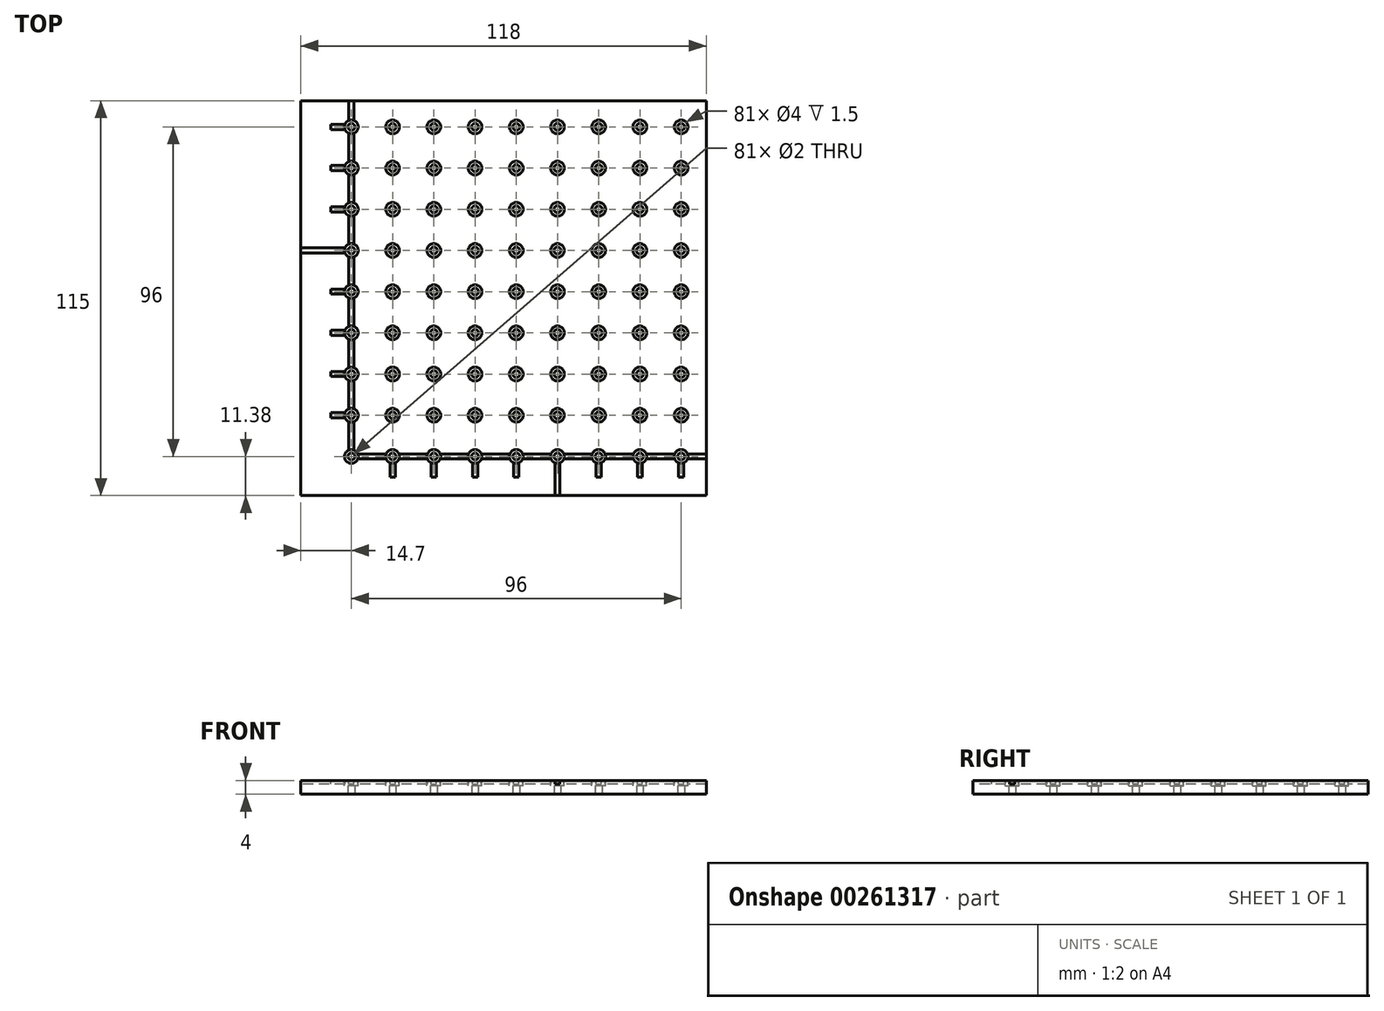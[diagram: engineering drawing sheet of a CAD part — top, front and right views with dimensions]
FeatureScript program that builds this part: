
annotation { "Feature Type Name" : "Feature", "Feature Type Description" : "" }
export const myFeature = defineFeature(function(context is Context, id is Id, definition is map)
    precondition{}
    {
        {
            var Q0;
            Q0=qCreatedBy(makeId("Top.planeOp"),FACE);
            var sketch = newSketch(context, id + "F0", { "sketchPlane" : qUnion([Q0])});
            skLineSegment(sketch, "E0.bottom", {"start": v(-95, -95) * mm, "end": v(95, -95) * mm});
            skLineSegment(sketch, "E0.top", {"start": v(-95, 95) * mm, "end": v(95, 95) * mm});
            skLineSegment(sketch, "E0.left", {"start": v(-95, -95) * mm, "end": v(-95, 95) * mm});
            skLineSegment(sketch, "E0.right", {"start": v(95, -95) * mm, "end": v(95, 95) * mm});
            skPoint(sketch, "E0.middle", {"position": v(0, 0) * mm});
            skCircle(sketch, "E1", {"center": v(-80, 85) * mm, "radius": 1 * mm});
            skCircle(sketch, "E2.0.1.0", {"center": v(-80, 73) * mm, "radius": 1 * mm});
            skCircle(sketch, "E2.0.2.0", {"center": v(-80, 61) * mm, "radius": 1 * mm});
            skCircle(sketch, "E2.0.3.0", {"center": v(-80, 49) * mm, "radius": 1 * mm});
            skCircle(sketch, "E2.0.4.0", {"center": v(-80, 37) * mm, "radius": 1 * mm});
            skCircle(sketch, "E2.0.5.0", {"center": v(-80, 25) * mm, "radius": 1 * mm});
            skCircle(sketch, "E2.0.6.0", {"center": v(-80, 13) * mm, "radius": 1 * mm});
            skCircle(sketch, "E2.0.7.0", {"center": v(-80, 1) * mm, "radius": 1 * mm});
            skCircle(sketch, "E2.0.8.0", {"center": v(-80, -11) * mm, "radius": 1 * mm});
            skCircle(sketch, "E2.0.9.0", {"center": v(-80, -23) * mm, "radius": 1 * mm});
            skCircle(sketch, "E2.0.10.0", {"center": v(-80, -35) * mm, "radius": 1 * mm});
            skCircle(sketch, "E2.0.11.0", {"center": v(-80, -47) * mm, "radius": 1 * mm});
            skCircle(sketch, "E2.0.12.0", {"center": v(-80, -59) * mm, "radius": 1 * mm});
            skCircle(sketch, "E2.0.13.0", {"center": v(-80, -71) * mm, "radius": 1 * mm});
            skCircle(sketch, "E2.0.14.0", {"center": v(-80, -83) * mm, "radius": 1 * mm});
            skLineSegment(sketch, "E2.direction1", {"start": v(-80, 85) * mm, "end": v(-68, 85) * mm, "construction": true});
            skLineSegment(sketch, "E2.direction2", {"start": v(-80, 85) * mm, "end": v(-80, 73) * mm, "construction": true});
            skCircle(sketch, "E3.0.1.0", {"center": v(-68, 85) * mm, "radius": 1 * mm});
            skCircle(sketch, "E3.0.1.1", {"center": v(-68, 73) * mm, "radius": 1 * mm});
            skCircle(sketch, "E3.0.1.2", {"center": v(-68, 61) * mm, "radius": 1 * mm});
            skCircle(sketch, "E3.0.1.3", {"center": v(-68, 49) * mm, "radius": 1 * mm});
            skCircle(sketch, "E3.0.1.4", {"center": v(-68, 37) * mm, "radius": 1 * mm});
            skCircle(sketch, "E3.0.1.5", {"center": v(-68, 25) * mm, "radius": 1 * mm});
            skCircle(sketch, "E3.0.1.6", {"center": v(-68, 13) * mm, "radius": 1 * mm});
            skCircle(sketch, "E3.0.1.7", {"center": v(-68, 1) * mm, "radius": 1 * mm});
            skCircle(sketch, "E3.0.1.8", {"center": v(-68, -11) * mm, "radius": 1 * mm});
            skCircle(sketch, "E3.0.1.9", {"center": v(-68, -23) * mm, "radius": 1 * mm});
            skCircle(sketch, "E3.0.1.10", {"center": v(-68, -35) * mm, "radius": 1 * mm});
            skCircle(sketch, "E3.0.1.11", {"center": v(-68, -47) * mm, "radius": 1 * mm});
            skCircle(sketch, "E3.0.1.12", {"center": v(-68, -59) * mm, "radius": 1 * mm});
            skCircle(sketch, "E3.0.1.13", {"center": v(-68, -71) * mm, "radius": 1 * mm});
            skCircle(sketch, "E3.0.1.14", {"center": v(-68, -83) * mm, "radius": 1 * mm});
            skCircle(sketch, "E3.0.2.0", {"center": v(-56, 85) * mm, "radius": 1 * mm});
            skCircle(sketch, "E3.0.2.1", {"center": v(-56, 73) * mm, "radius": 1 * mm});
            skCircle(sketch, "E3.0.2.2", {"center": v(-56, 61) * mm, "radius": 1 * mm});
            skCircle(sketch, "E3.0.2.3", {"center": v(-56, 49) * mm, "radius": 1 * mm});
            skCircle(sketch, "E3.0.2.4", {"center": v(-56, 37) * mm, "radius": 1 * mm});
            skCircle(sketch, "E3.0.2.5", {"center": v(-56, 25) * mm, "radius": 1 * mm});
            skCircle(sketch, "E3.0.2.6", {"center": v(-56, 13) * mm, "radius": 1 * mm});
            skCircle(sketch, "E3.0.2.7", {"center": v(-56, 1) * mm, "radius": 1 * mm});
            skCircle(sketch, "E3.0.2.8", {"center": v(-56, -11) * mm, "radius": 1 * mm});
            skCircle(sketch, "E3.0.2.9", {"center": v(-56, -23) * mm, "radius": 1 * mm});
            skCircle(sketch, "E3.0.2.10", {"center": v(-56, -35) * mm, "radius": 1 * mm});
            skCircle(sketch, "E3.0.2.11", {"center": v(-56, -47) * mm, "radius": 1 * mm});
            skCircle(sketch, "E3.0.2.12", {"center": v(-56, -59) * mm, "radius": 1 * mm});
            skCircle(sketch, "E3.0.2.13", {"center": v(-56, -71) * mm, "radius": 1 * mm});
            skCircle(sketch, "E3.0.2.14", {"center": v(-56, -83) * mm, "radius": 1 * mm});
            skCircle(sketch, "E3.0.3.0", {"center": v(-44, 85) * mm, "radius": 1 * mm});
            skCircle(sketch, "E3.0.3.1", {"center": v(-44, 73) * mm, "radius": 1 * mm});
            skCircle(sketch, "E3.0.3.2", {"center": v(-44, 61) * mm, "radius": 1 * mm});
            skCircle(sketch, "E3.0.3.3", {"center": v(-44, 49) * mm, "radius": 1 * mm});
            skCircle(sketch, "E3.0.3.4", {"center": v(-44, 37) * mm, "radius": 1 * mm});
            skCircle(sketch, "E3.0.3.5", {"center": v(-44, 25) * mm, "radius": 1 * mm});
            skCircle(sketch, "E3.0.3.6", {"center": v(-44, 13) * mm, "radius": 1 * mm});
            skCircle(sketch, "E3.0.3.7", {"center": v(-44, 1) * mm, "radius": 1 * mm});
            skCircle(sketch, "E3.0.3.8", {"center": v(-44, -11) * mm, "radius": 1 * mm});
            skCircle(sketch, "E3.0.3.9", {"center": v(-44, -23) * mm, "radius": 1 * mm});
            skCircle(sketch, "E3.0.3.10", {"center": v(-44, -35) * mm, "radius": 1 * mm});
            skCircle(sketch, "E3.0.3.11", {"center": v(-44, -47) * mm, "radius": 1 * mm});
            skCircle(sketch, "E3.0.3.12", {"center": v(-44, -59) * mm, "radius": 1 * mm});
            skCircle(sketch, "E3.0.3.13", {"center": v(-44, -71) * mm, "radius": 1 * mm});
            skCircle(sketch, "E3.0.3.14", {"center": v(-44, -83) * mm, "radius": 1 * mm});
            skCircle(sketch, "E3.0.4.0", {"center": v(-32, 85) * mm, "radius": 1 * mm});
            skCircle(sketch, "E3.0.4.1", {"center": v(-32, 73) * mm, "radius": 1 * mm});
            skCircle(sketch, "E3.0.4.2", {"center": v(-32, 61) * mm, "radius": 1 * mm});
            skCircle(sketch, "E3.0.4.3", {"center": v(-32, 49) * mm, "radius": 1 * mm});
            skCircle(sketch, "E3.0.4.4", {"center": v(-32, 37) * mm, "radius": 1 * mm});
            skCircle(sketch, "E3.0.4.5", {"center": v(-32, 25) * mm, "radius": 1 * mm});
            skCircle(sketch, "E3.0.4.6", {"center": v(-32, 13) * mm, "radius": 1 * mm});
            skCircle(sketch, "E3.0.4.7", {"center": v(-32, 1) * mm, "radius": 1 * mm});
            skCircle(sketch, "E3.0.4.8", {"center": v(-32, -11) * mm, "radius": 1 * mm});
            skCircle(sketch, "E3.0.4.9", {"center": v(-32, -23) * mm, "radius": 1 * mm});
            skCircle(sketch, "E3.0.4.10", {"center": v(-32, -35) * mm, "radius": 1 * mm});
            skCircle(sketch, "E3.0.4.11", {"center": v(-32, -47) * mm, "radius": 1 * mm});
            skCircle(sketch, "E3.0.4.12", {"center": v(-32, -59) * mm, "radius": 1 * mm});
            skCircle(sketch, "E3.0.4.13", {"center": v(-32, -71) * mm, "radius": 1 * mm});
            skCircle(sketch, "E3.0.4.14", {"center": v(-32, -83) * mm, "radius": 1 * mm});
            skCircle(sketch, "E3.0.5.0", {"center": v(-20, 85) * mm, "radius": 1 * mm});
            skCircle(sketch, "E3.0.5.1", {"center": v(-20, 73) * mm, "radius": 1 * mm});
            skCircle(sketch, "E3.0.5.2", {"center": v(-20, 61) * mm, "radius": 1 * mm});
            skCircle(sketch, "E3.0.5.3", {"center": v(-20, 49) * mm, "radius": 1 * mm});
            skCircle(sketch, "E3.0.5.4", {"center": v(-20, 37) * mm, "radius": 1 * mm});
            skCircle(sketch, "E3.0.5.5", {"center": v(-20, 25) * mm, "radius": 1 * mm});
            skCircle(sketch, "E3.0.5.6", {"center": v(-20, 13) * mm, "radius": 1 * mm});
            skCircle(sketch, "E3.0.5.7", {"center": v(-20, 1) * mm, "radius": 1 * mm});
            skCircle(sketch, "E3.0.5.8", {"center": v(-20, -11) * mm, "radius": 1 * mm});
            skCircle(sketch, "E3.0.5.9", {"center": v(-20, -23) * mm, "radius": 1 * mm});
            skCircle(sketch, "E3.0.5.10", {"center": v(-20, -35) * mm, "radius": 1 * mm});
            skCircle(sketch, "E3.0.5.11", {"center": v(-20, -47) * mm, "radius": 1 * mm});
            skCircle(sketch, "E3.0.5.12", {"center": v(-20, -59) * mm, "radius": 1 * mm});
            skCircle(sketch, "E3.0.5.13", {"center": v(-20, -71) * mm, "radius": 1 * mm});
            skCircle(sketch, "E3.0.5.14", {"center": v(-20, -83) * mm, "radius": 1 * mm});
            skCircle(sketch, "E3.0.6.0", {"center": v(-8, 85) * mm, "radius": 1 * mm});
            skCircle(sketch, "E3.0.6.1", {"center": v(-8, 73) * mm, "radius": 1 * mm});
            skCircle(sketch, "E3.0.6.2", {"center": v(-8, 61) * mm, "radius": 1 * mm});
            skCircle(sketch, "E3.0.6.3", {"center": v(-8, 49) * mm, "radius": 1 * mm});
            skCircle(sketch, "E3.0.6.4", {"center": v(-8, 37) * mm, "radius": 1 * mm});
            skCircle(sketch, "E3.0.6.5", {"center": v(-8, 25) * mm, "radius": 1 * mm});
            skCircle(sketch, "E3.0.6.6", {"center": v(-8, 13) * mm, "radius": 1 * mm});
            skCircle(sketch, "E3.0.6.7", {"center": v(-8, 1) * mm, "radius": 1 * mm});
            skCircle(sketch, "E3.0.6.8", {"center": v(-8, -11) * mm, "radius": 1 * mm});
            skCircle(sketch, "E3.0.6.9", {"center": v(-8, -23) * mm, "radius": 1 * mm});
            skCircle(sketch, "E3.0.6.10", {"center": v(-8, -35) * mm, "radius": 1 * mm});
            skCircle(sketch, "E3.0.6.11", {"center": v(-8, -47) * mm, "radius": 1 * mm});
            skCircle(sketch, "E3.0.6.12", {"center": v(-8, -59) * mm, "radius": 1 * mm});
            skCircle(sketch, "E3.0.6.13", {"center": v(-8, -71) * mm, "radius": 1 * mm});
            skCircle(sketch, "E3.0.6.14", {"center": v(-8, -83) * mm, "radius": 1 * mm});
            skCircle(sketch, "E3.0.7.0", {"center": v(4, 85) * mm, "radius": 1 * mm});
            skCircle(sketch, "E3.0.7.1", {"center": v(4, 73) * mm, "radius": 1 * mm});
            skCircle(sketch, "E3.0.7.2", {"center": v(4, 61) * mm, "radius": 1 * mm});
            skCircle(sketch, "E3.0.7.3", {"center": v(4, 49) * mm, "radius": 1 * mm});
            skCircle(sketch, "E3.0.7.4", {"center": v(4, 37) * mm, "radius": 1 * mm});
            skCircle(sketch, "E3.0.7.5", {"center": v(4, 25) * mm, "radius": 1 * mm});
            skCircle(sketch, "E3.0.7.6", {"center": v(4, 13) * mm, "radius": 1 * mm});
            skCircle(sketch, "E3.0.7.7", {"center": v(4, 1) * mm, "radius": 1 * mm});
            skCircle(sketch, "E3.0.7.8", {"center": v(4, -11) * mm, "radius": 1 * mm});
            skCircle(sketch, "E3.0.7.9", {"center": v(4, -23) * mm, "radius": 1 * mm});
            skCircle(sketch, "E3.0.7.10", {"center": v(4, -35) * mm, "radius": 1 * mm});
            skCircle(sketch, "E3.0.7.11", {"center": v(4, -47) * mm, "radius": 1 * mm});
            skCircle(sketch, "E3.0.7.12", {"center": v(4, -59) * mm, "radius": 1 * mm});
            skCircle(sketch, "E3.0.7.13", {"center": v(4, -71) * mm, "radius": 1 * mm});
            skCircle(sketch, "E3.0.7.14", {"center": v(4, -83) * mm, "radius": 1 * mm});
            skCircle(sketch, "E3.0.8.0", {"center": v(16, 85) * mm, "radius": 1 * mm});
            skCircle(sketch, "E3.0.8.1", {"center": v(16, 73) * mm, "radius": 1 * mm});
            skCircle(sketch, "E3.0.8.2", {"center": v(16, 61) * mm, "radius": 1 * mm});
            skCircle(sketch, "E3.0.8.3", {"center": v(16, 49) * mm, "radius": 1 * mm});
            skCircle(sketch, "E3.0.8.4", {"center": v(16, 37) * mm, "radius": 1 * mm});
            skCircle(sketch, "E3.0.8.5", {"center": v(16, 25) * mm, "radius": 1 * mm});
            skCircle(sketch, "E3.0.8.6", {"center": v(16, 13) * mm, "radius": 1 * mm});
            skCircle(sketch, "E3.0.8.7", {"center": v(16, 1) * mm, "radius": 1 * mm});
            skCircle(sketch, "E3.0.8.8", {"center": v(16, -11) * mm, "radius": 1 * mm});
            skCircle(sketch, "E3.0.8.9", {"center": v(16, -23) * mm, "radius": 1 * mm});
            skCircle(sketch, "E3.0.8.10", {"center": v(16, -35) * mm, "radius": 1 * mm});
            skCircle(sketch, "E3.0.8.11", {"center": v(16, -47) * mm, "radius": 1 * mm});
            skCircle(sketch, "E3.0.8.12", {"center": v(16, -59) * mm, "radius": 1 * mm});
            skCircle(sketch, "E3.0.8.13", {"center": v(16, -71) * mm, "radius": 1 * mm});
            skCircle(sketch, "E3.0.8.14", {"center": v(16, -83) * mm, "radius": 1 * mm});
            skCircle(sketch, "E3.0.9.0", {"center": v(28, 85) * mm, "radius": 1 * mm});
            skCircle(sketch, "E3.0.9.1", {"center": v(28, 73) * mm, "radius": 1 * mm});
            skCircle(sketch, "E3.0.9.2", {"center": v(28, 61) * mm, "radius": 1 * mm});
            skCircle(sketch, "E3.0.9.3", {"center": v(28, 49) * mm, "radius": 1 * mm});
            skCircle(sketch, "E3.0.9.4", {"center": v(28, 37) * mm, "radius": 1 * mm});
            skCircle(sketch, "E3.0.9.5", {"center": v(28, 25) * mm, "radius": 1 * mm});
            skCircle(sketch, "E3.0.9.6", {"center": v(28, 13) * mm, "radius": 1 * mm});
            skCircle(sketch, "E3.0.9.7", {"center": v(28, 1) * mm, "radius": 1 * mm});
            skCircle(sketch, "E3.0.9.8", {"center": v(28, -11) * mm, "radius": 1 * mm});
            skCircle(sketch, "E3.0.9.9", {"center": v(28, -23) * mm, "radius": 1 * mm});
            skCircle(sketch, "E3.0.9.10", {"center": v(28, -35) * mm, "radius": 1 * mm});
            skCircle(sketch, "E3.0.9.11", {"center": v(28, -47) * mm, "radius": 1 * mm});
            skCircle(sketch, "E3.0.9.12", {"center": v(28, -59) * mm, "radius": 1 * mm});
            skCircle(sketch, "E3.0.9.13", {"center": v(28, -71) * mm, "radius": 1 * mm});
            skCircle(sketch, "E3.0.9.14", {"center": v(28, -83) * mm, "radius": 1 * mm});
            skCircle(sketch, "E3.0.10.0", {"center": v(40, 85) * mm, "radius": 1 * mm});
            skCircle(sketch, "E3.0.10.1", {"center": v(40, 73) * mm, "radius": 1 * mm});
            skCircle(sketch, "E3.0.10.2", {"center": v(40, 61) * mm, "radius": 1 * mm});
            skCircle(sketch, "E3.0.10.3", {"center": v(40, 49) * mm, "radius": 1 * mm});
            skCircle(sketch, "E3.0.10.4", {"center": v(40, 37) * mm, "radius": 1 * mm});
            skCircle(sketch, "E3.0.10.5", {"center": v(40, 25) * mm, "radius": 1 * mm});
            skCircle(sketch, "E3.0.10.6", {"center": v(40, 13) * mm, "radius": 1 * mm});
            skCircle(sketch, "E3.0.10.7", {"center": v(40, 1) * mm, "radius": 1 * mm});
            skCircle(sketch, "E3.0.10.8", {"center": v(40, -11) * mm, "radius": 1 * mm});
            skCircle(sketch, "E3.0.10.9", {"center": v(40, -23) * mm, "radius": 1 * mm});
            skCircle(sketch, "E3.0.10.10", {"center": v(40, -35) * mm, "radius": 1 * mm});
            skCircle(sketch, "E3.0.10.11", {"center": v(40, -47) * mm, "radius": 1 * mm});
            skCircle(sketch, "E3.0.10.12", {"center": v(40, -59) * mm, "radius": 1 * mm});
            skCircle(sketch, "E3.0.10.13", {"center": v(40, -71) * mm, "radius": 1 * mm});
            skCircle(sketch, "E3.0.10.14", {"center": v(40, -83) * mm, "radius": 1 * mm});
            skCircle(sketch, "E3.0.11.0", {"center": v(52, 85) * mm, "radius": 1 * mm});
            skCircle(sketch, "E3.0.11.1", {"center": v(52, 73) * mm, "radius": 1 * mm});
            skCircle(sketch, "E3.0.11.2", {"center": v(52, 61) * mm, "radius": 1 * mm});
            skCircle(sketch, "E3.0.11.3", {"center": v(52, 49) * mm, "radius": 1 * mm});
            skCircle(sketch, "E3.0.11.4", {"center": v(52, 37) * mm, "radius": 1 * mm});
            skCircle(sketch, "E3.0.11.5", {"center": v(52, 25) * mm, "radius": 1 * mm});
            skCircle(sketch, "E3.0.11.6", {"center": v(52, 13) * mm, "radius": 1 * mm});
            skCircle(sketch, "E3.0.11.7", {"center": v(52, 1) * mm, "radius": 1 * mm});
            skCircle(sketch, "E3.0.11.8", {"center": v(52, -11) * mm, "radius": 1 * mm});
            skCircle(sketch, "E3.0.11.9", {"center": v(52, -23) * mm, "radius": 1 * mm});
            skCircle(sketch, "E3.0.11.10", {"center": v(52, -35) * mm, "radius": 1 * mm});
            skCircle(sketch, "E3.0.11.11", {"center": v(52, -47) * mm, "radius": 1 * mm});
            skCircle(sketch, "E3.0.11.12", {"center": v(52, -59) * mm, "radius": 1 * mm});
            skCircle(sketch, "E3.0.11.13", {"center": v(52, -71) * mm, "radius": 1 * mm});
            skCircle(sketch, "E3.0.11.14", {"center": v(52, -83) * mm, "radius": 1 * mm});
            skCircle(sketch, "E3.0.12.0", {"center": v(64, 85) * mm, "radius": 1 * mm});
            skCircle(sketch, "E3.0.12.1", {"center": v(64, 73) * mm, "radius": 1 * mm});
            skCircle(sketch, "E3.0.12.2", {"center": v(64, 61) * mm, "radius": 1 * mm});
            skCircle(sketch, "E3.0.12.3", {"center": v(64, 49) * mm, "radius": 1 * mm});
            skCircle(sketch, "E3.0.12.4", {"center": v(64, 37) * mm, "radius": 1 * mm});
            skCircle(sketch, "E3.0.12.5", {"center": v(64, 25) * mm, "radius": 1 * mm});
            skCircle(sketch, "E3.0.12.6", {"center": v(64, 13) * mm, "radius": 1 * mm});
            skCircle(sketch, "E3.0.12.7", {"center": v(64, 1) * mm, "radius": 1 * mm});
            skCircle(sketch, "E3.0.12.8", {"center": v(64, -11) * mm, "radius": 1 * mm});
            skCircle(sketch, "E3.0.12.9", {"center": v(64, -23) * mm, "radius": 1 * mm});
            skCircle(sketch, "E3.0.12.10", {"center": v(64, -35) * mm, "radius": 1 * mm});
            skCircle(sketch, "E3.0.12.11", {"center": v(64, -47) * mm, "radius": 1 * mm});
            skCircle(sketch, "E3.0.12.12", {"center": v(64, -59) * mm, "radius": 1 * mm});
            skCircle(sketch, "E3.0.12.13", {"center": v(64, -71) * mm, "radius": 1 * mm});
            skCircle(sketch, "E3.0.12.14", {"center": v(64, -83) * mm, "radius": 1 * mm});
            skCircle(sketch, "E3.0.13.0", {"center": v(76, 85) * mm, "radius": 1 * mm});
            skCircle(sketch, "E3.0.13.1", {"center": v(76, 73) * mm, "radius": 1 * mm});
            skCircle(sketch, "E3.0.13.2", {"center": v(76, 61) * mm, "radius": 1 * mm});
            skCircle(sketch, "E3.0.13.3", {"center": v(76, 49) * mm, "radius": 1 * mm});
            skCircle(sketch, "E3.0.13.4", {"center": v(76, 37) * mm, "radius": 1 * mm});
            skCircle(sketch, "E3.0.13.5", {"center": v(76, 25) * mm, "radius": 1 * mm});
            skCircle(sketch, "E3.0.13.6", {"center": v(76, 13) * mm, "radius": 1 * mm});
            skCircle(sketch, "E3.0.13.7", {"center": v(76, 1) * mm, "radius": 1 * mm});
            skCircle(sketch, "E3.0.13.8", {"center": v(76, -11) * mm, "radius": 1 * mm});
            skCircle(sketch, "E3.0.13.9", {"center": v(76, -23) * mm, "radius": 1 * mm});
            skCircle(sketch, "E3.0.13.10", {"center": v(76, -35) * mm, "radius": 1 * mm});
            skCircle(sketch, "E3.0.13.11", {"center": v(76, -47) * mm, "radius": 1 * mm});
            skCircle(sketch, "E3.0.13.12", {"center": v(76, -59) * mm, "radius": 1 * mm});
            skCircle(sketch, "E3.0.13.13", {"center": v(76, -71) * mm, "radius": 1 * mm});
            skCircle(sketch, "E3.0.13.14", {"center": v(76, -83) * mm, "radius": 1 * mm});
            skCircle(sketch, "E3.0.14.0", {"center": v(88, 85) * mm, "radius": 1 * mm});
            skCircle(sketch, "E3.0.14.1", {"center": v(88, 73) * mm, "radius": 1 * mm});
            skCircle(sketch, "E3.0.14.2", {"center": v(88, 61) * mm, "radius": 1 * mm});
            skCircle(sketch, "E3.0.14.3", {"center": v(88, 49) * mm, "radius": 1 * mm});
            skCircle(sketch, "E3.0.14.4", {"center": v(88, 37) * mm, "radius": 1 * mm});
            skCircle(sketch, "E3.0.14.5", {"center": v(88, 25) * mm, "radius": 1 * mm});
            skCircle(sketch, "E3.0.14.6", {"center": v(88, 13) * mm, "radius": 1 * mm});
            skCircle(sketch, "E3.0.14.7", {"center": v(88, 1) * mm, "radius": 1 * mm});
            skCircle(sketch, "E3.0.14.8", {"center": v(88, -11) * mm, "radius": 1 * mm});
            skCircle(sketch, "E3.0.14.9", {"center": v(88, -23) * mm, "radius": 1 * mm});
            skCircle(sketch, "E3.0.14.10", {"center": v(88, -35) * mm, "radius": 1 * mm});
            skCircle(sketch, "E3.0.14.11", {"center": v(88, -47) * mm, "radius": 1 * mm});
            skCircle(sketch, "E3.0.14.12", {"center": v(88, -59) * mm, "radius": 1 * mm});
            skCircle(sketch, "E3.0.14.13", {"center": v(88, -71) * mm, "radius": 1 * mm});
            skCircle(sketch, "E3.0.14.14", {"center": v(88, -83) * mm, "radius": 1 * mm});
            skSolve(sketch);
        }
        {
            var Q0;
            Q0 = qSketchRegion(id + "F0", true);
            extrude(context, id + "F1", {"entities" : qUnion([Q0]), "depth" : 4 * mm});
        }
        {
            var Q0;
            Q0=makeQuery(id+"F1.opExtrude","CAP_FACE",FACE,{"disambiguationData":[OSD([sQuery(id+"F0.wireOp",EDGE,"E0.bottom"),sQuery(id+"F0.wireOp",EDGE,"E0.top"),sQuery(id+"F0.wireOp",EDGE,"E0.left"),sQuery(id+"F0.wireOp",EDGE,"E0.right"),sQuery(id+"F0.wireOp",EDGE,"E1"),sQuery(id+"F0.wireOp",EDGE,"E2.0.1.0"),sQuery(id+"F0.wireOp",EDGE,"E2.0.2.0"),sQuery(id+"F0.wireOp",EDGE,"E2.0.3.0"),sQuery(id+"F0.wireOp",EDGE,"E2.0.4.0"),sQuery(id+"F0.wireOp",EDGE,"E2.0.5.0"),sQuery(id+"F0.wireOp",EDGE,"E2.0.6.0"),sQuery(id+"F0.wireOp",EDGE,"E2.0.7.0"),sQuery(id+"F0.wireOp",EDGE,"E2.0.8.0"),sQuery(id+"F0.wireOp",EDGE,"E2.0.9.0"),sQuery(id+"F0.wireOp",EDGE,"E2.0.10.0"),sQuery(id+"F0.wireOp",EDGE,"E2.0.11.0"),sQuery(id+"F0.wireOp",EDGE,"E2.0.12.0"),sQuery(id+"F0.wireOp",EDGE,"E2.0.13.0"),sQuery(id+"F0.wireOp",EDGE,"E2.0.14.0"),sQuery(id+"F0.wireOp",EDGE,"E2.0.15.0"),sQuery(id+"F0.wireOp",EDGE,"E2.1.0.0"),sQuery(id+"F0.wireOp",EDGE,"E2.1.1.0"),sQuery(id+"F0.wireOp",EDGE,"E2.1.2.0"),sQuery(id+"F0.wireOp",EDGE,"E2.1.3.0"),sQuery(id+"F0.wireOp",EDGE,"E2.1.4.0"),sQuery(id+"F0.wireOp",EDGE,"E2.1.5.0"),sQuery(id+"F0.wireOp",EDGE,"E2.1.6.0"),sQuery(id+"F0.wireOp",EDGE,"E2.1.7.0"),sQuery(id+"F0.wireOp",EDGE,"E2.1.8.0"),sQuery(id+"F0.wireOp",EDGE,"E2.1.9.0"),sQuery(id+"F0.wireOp",EDGE,"E2.1.10.0"),sQuery(id+"F0.wireOp",EDGE,"E2.1.11.0"),sQuery(id+"F0.wireOp",EDGE,"E2.1.12.0"),sQuery(id+"F0.wireOp",EDGE,"E2.1.13.0"),sQuery(id+"F0.wireOp",EDGE,"E2.1.14.0"),sQuery(id+"F0.wireOp",EDGE,"E2.1.15.0"),sQuery(id+"F0.wireOp",EDGE,"E2.2.0.0"),sQuery(id+"F0.wireOp",EDGE,"E2.2.1.0"),sQuery(id+"F0.wireOp",EDGE,"E2.2.2.0"),sQuery(id+"F0.wireOp",EDGE,"E2.2.3.0"),sQuery(id+"F0.wireOp",EDGE,"E2.2.4.0"),sQuery(id+"F0.wireOp",EDGE,"E2.2.5.0"),sQuery(id+"F0.wireOp",EDGE,"E2.2.6.0"),sQuery(id+"F0.wireOp",EDGE,"E2.2.7.0"),sQuery(id+"F0.wireOp",EDGE,"E2.2.8.0"),sQuery(id+"F0.wireOp",EDGE,"E2.2.9.0"),sQuery(id+"F0.wireOp",EDGE,"E2.2.10.0"),sQuery(id+"F0.wireOp",EDGE,"E2.2.11.0"),sQuery(id+"F0.wireOp",EDGE,"E2.2.12.0"),sQuery(id+"F0.wireOp",EDGE,"E2.2.13.0"),sQuery(id+"F0.wireOp",EDGE,"E2.2.14.0"),sQuery(id+"F0.wireOp",EDGE,"E2.2.15.0"),sQuery(id+"F0.wireOp",EDGE,"E2.3.0.0"),sQuery(id+"F0.wireOp",EDGE,"E2.3.1.0"),sQuery(id+"F0.wireOp",EDGE,"E2.3.11.0"),sQuery(id+"F0.wireOp",EDGE,"E2.3.12.0"),sQuery(id+"F0.wireOp",EDGE,"E2.3.13.0"),sQuery(id+"F0.wireOp",EDGE,"E2.3.14.0"),sQuery(id+"F0.wireOp",EDGE,"E2.3.15.0"),sQuery(id+"F0.wireOp",EDGE,"E2.4.0.0"),sQuery(id+"F0.wireOp",EDGE,"E2.4.1.0"),sQuery(id+"F0.wireOp",EDGE,"E2.4.2.0"),sQuery(id+"F0.wireOp",EDGE,"E2.4.11.0"),sQuery(id+"F0.wireOp",EDGE,"E2.4.12.0"),sQuery(id+"F0.wireOp",EDGE,"E2.4.13.0"),sQuery(id+"F0.wireOp",EDGE,"E2.4.14.0"),sQuery(id+"F0.wireOp",EDGE,"E2.4.15.0"),sQuery(id+"F0.wireOp",EDGE,"E2.5.0.0"),sQuery(id+"F0.wireOp",EDGE,"E2.5.1.0"),sQuery(id+"F0.wireOp",EDGE,"E2.5.11.0"),sQuery(id+"F0.wireOp",EDGE,"E2.5.12.0"),sQuery(id+"F0.wireOp",EDGE,"E2.5.13.0"),sQuery(id+"F0.wireOp",EDGE,"E2.5.14.0"),sQuery(id+"F0.wireOp",EDGE,"E2.5.15.0"),sQuery(id+"F0.wireOp",EDGE,"E2.6.0.0"),sQuery(id+"F0.wireOp",EDGE,"E2.6.1.0"),sQuery(id+"F0.wireOp",EDGE,"E2.6.2.0"),sQuery(id+"F0.wireOp",EDGE,"E2.6.11.0"),sQuery(id+"F0.wireOp",EDGE,"E2.6.12.0"),sQuery(id+"F0.wireOp",EDGE,"E2.6.13.0"),sQuery(id+"F0.wireOp",EDGE,"E2.6.14.0"),sQuery(id+"F0.wireOp",EDGE,"E2.6.15.0"),sQuery(id+"F0.wireOp",EDGE,"E2.7.0.0"),sQuery(id+"F0.wireOp",EDGE,"E2.7.1.0"),sQuery(id+"F0.wireOp",EDGE,"E2.7.2.0"),sQuery(id+"F0.wireOp",EDGE,"E2.7.3.0"),sQuery(id+"F0.wireOp",EDGE,"E2.7.4.0"),sQuery(id+"F0.wireOp",EDGE,"E2.7.5.0"),sQuery(id+"F0.wireOp",EDGE,"E2.7.6.0"),sQuery(id+"F0.wireOp",EDGE,"E2.7.7.0"),sQuery(id+"F0.wireOp",EDGE,"E2.7.8.0"),sQuery(id+"F0.wireOp",EDGE,"E2.7.9.0"),sQuery(id+"F0.wireOp",EDGE,"E2.7.10.0"),sQuery(id+"F0.wireOp",EDGE,"E2.7.11.0"),sQuery(id+"F0.wireOp",EDGE,"E2.7.12.0"),sQuery(id+"F0.wireOp",EDGE,"E2.7.13.0"),sQuery(id+"F0.wireOp",EDGE,"E2.7.14.0"),sQuery(id+"F0.wireOp",EDGE,"E2.7.15.0"),sQuery(id+"F0.wireOp",EDGE,"E2.8.0.0"),sQuery(id+"F0.wireOp",EDGE,"E2.8.1.0"),sQuery(id+"F0.wireOp",EDGE,"E2.8.2.0"),sQuery(id+"F0.wireOp",EDGE,"E2.8.3.0"),sQuery(id+"F0.wireOp",EDGE,"E2.8.4.0"),sQuery(id+"F0.wireOp",EDGE,"E2.8.5.0"),sQuery(id+"F0.wireOp",EDGE,"E2.8.6.0"),sQuery(id+"F0.wireOp",EDGE,"E2.8.7.0"),sQuery(id+"F0.wireOp",EDGE,"E2.8.8.0"),sQuery(id+"F0.wireOp",EDGE,"E2.8.9.0"),sQuery(id+"F0.wireOp",EDGE,"E2.8.10.0"),sQuery(id+"F0.wireOp",EDGE,"E2.8.11.0"),sQuery(id+"F0.wireOp",EDGE,"E2.8.12.0"),sQuery(id+"F0.wireOp",EDGE,"E2.8.13.0"),sQuery(id+"F0.wireOp",EDGE,"E2.8.14.0"),sQuery(id+"F0.wireOp",EDGE,"E2.8.15.0"),sQuery(id+"F0.wireOp",EDGE,"E2.9.0.0"),sQuery(id+"F0.wireOp",EDGE,"E2.9.1.0"),sQuery(id+"F0.wireOp",EDGE,"E2.9.2.0"),sQuery(id+"F0.wireOp",EDGE,"E2.9.3.0"),sQuery(id+"F0.wireOp",EDGE,"E2.9.4.0"),sQuery(id+"F0.wireOp",EDGE,"E2.9.5.0"),sQuery(id+"F0.wireOp",EDGE,"E2.9.6.0"),sQuery(id+"F0.wireOp",EDGE,"E2.9.7.0"),sQuery(id+"F0.wireOp",EDGE,"E2.9.8.0"),sQuery(id+"F0.wireOp",EDGE,"E2.9.9.0"),sQuery(id+"F0.wireOp",EDGE,"E2.9.10.0"),sQuery(id+"F0.wireOp",EDGE,"E2.9.11.0"),sQuery(id+"F0.wireOp",EDGE,"E2.9.12.0"),sQuery(id+"F0.wireOp",EDGE,"E2.9.13.0"),sQuery(id+"F0.wireOp",EDGE,"E2.9.14.0"),sQuery(id+"F0.wireOp",EDGE,"E2.9.15.0"),sQuery(id+"F0.wireOp",EDGE,"E2.10.0.0"),sQuery(id+"F0.wireOp",EDGE,"E2.10.1.0"),sQuery(id+"F0.wireOp",EDGE,"E2.10.2.0"),sQuery(id+"F0.wireOp",EDGE,"E2.10.3.0"),sQuery(id+"F0.wireOp",EDGE,"E2.10.4.0"),sQuery(id+"F0.wireOp",EDGE,"E2.10.5.0"),sQuery(id+"F0.wireOp",EDGE,"E2.10.6.0"),sQuery(id+"F0.wireOp",EDGE,"E2.10.7.0"),sQuery(id+"F0.wireOp",EDGE,"E2.10.8.0"),sQuery(id+"F0.wireOp",EDGE,"E2.10.9.0"),sQuery(id+"F0.wireOp",EDGE,"E2.10.10.0"),sQuery(id+"F0.wireOp",EDGE,"E2.10.11.0"),sQuery(id+"F0.wireOp",EDGE,"E2.10.12.0"),sQuery(id+"F0.wireOp",EDGE,"E2.10.13.0"),sQuery(id+"F0.wireOp",EDGE,"E2.10.14.0"),sQuery(id+"F0.wireOp",EDGE,"E2.10.15.0"),sQuery(id+"F0.wireOp",EDGE,"E2.11.0.0"),sQuery(id+"F0.wireOp",EDGE,"E2.11.1.0"),sQuery(id+"F0.wireOp",EDGE,"E2.11.2.0"),sQuery(id+"F0.wireOp",EDGE,"E2.11.3.0"),sQuery(id+"F0.wireOp",EDGE,"E2.11.4.0"),sQuery(id+"F0.wireOp",EDGE,"E2.11.5.0"),sQuery(id+"F0.wireOp",EDGE,"E2.11.6.0"),sQuery(id+"F0.wireOp",EDGE,"E2.11.7.0"),sQuery(id+"F0.wireOp",EDGE,"E2.11.8.0"),sQuery(id+"F0.wireOp",EDGE,"E2.11.9.0"),sQuery(id+"F0.wireOp",EDGE,"E2.11.10.0"),sQuery(id+"F0.wireOp",EDGE,"E2.11.11.0"),sQuery(id+"F0.wireOp",EDGE,"E2.11.12.0"),sQuery(id+"F0.wireOp",EDGE,"E2.11.13.0"),sQuery(id+"F0.wireOp",EDGE,"E2.11.14.0"),sQuery(id+"F0.wireOp",EDGE,"E2.11.15.0"),sQuery(id+"F0.wireOp",EDGE,"E2.12.0.0"),sQuery(id+"F0.wireOp",EDGE,"E2.12.1.0"),sQuery(id+"F0.wireOp",EDGE,"E2.12.2.0"),sQuery(id+"F0.wireOp",EDGE,"E2.12.3.0"),sQuery(id+"F0.wireOp",EDGE,"E2.12.4.0"),sQuery(id+"F0.wireOp",EDGE,"E2.12.5.0"),sQuery(id+"F0.wireOp",EDGE,"E2.12.6.0"),sQuery(id+"F0.wireOp",EDGE,"E2.12.7.0"),sQuery(id+"F0.wireOp",EDGE,"E2.12.8.0"),sQuery(id+"F0.wireOp",EDGE,"E2.12.9.0"),sQuery(id+"F0.wireOp",EDGE,"E2.12.10.0"),sQuery(id+"F0.wireOp",EDGE,"E2.12.11.0"),sQuery(id+"F0.wireOp",EDGE,"E2.12.12.0"),sQuery(id+"F0.wireOp",EDGE,"E2.12.13.0"),sQuery(id+"F0.wireOp",EDGE,"E2.12.14.0"),sQuery(id+"F0.wireOp",EDGE,"E2.12.15.0"),sQuery(id+"F0.wireOp",EDGE,"E2.13.0.0"),sQuery(id+"F0.wireOp",EDGE,"E2.13.1.0"),sQuery(id+"F0.wireOp",EDGE,"E2.13.2.0"),sQuery(id+"F0.wireOp",EDGE,"E2.13.3.0"),sQuery(id+"F0.wireOp",EDGE,"E2.13.4.0"),sQuery(id+"F0.wireOp",EDGE,"E2.13.5.0"),sQuery(id+"F0.wireOp",EDGE,"E2.13.6.0"),sQuery(id+"F0.wireOp",EDGE,"E2.13.7.0"),sQuery(id+"F0.wireOp",EDGE,"E2.13.8.0"),sQuery(id+"F0.wireOp",EDGE,"E2.13.9.0"),sQuery(id+"F0.wireOp",EDGE,"E2.13.10.0"),sQuery(id+"F0.wireOp",EDGE,"E2.13.11.0"),sQuery(id+"F0.wireOp",EDGE,"E2.13.12.0"),sQuery(id+"F0.wireOp",EDGE,"E2.13.13.0"),sQuery(id+"F0.wireOp",EDGE,"E2.13.14.0"),sQuery(id+"F0.wireOp",EDGE,"E2.13.15.0"),sQuery(id+"F0.wireOp",EDGE,"E2.14.0.0"),sQuery(id+"F0.wireOp",EDGE,"E2.14.1.0"),sQuery(id+"F0.wireOp",EDGE,"E2.14.2.0"),sQuery(id+"F0.wireOp",EDGE,"E2.14.3.0"),sQuery(id+"F0.wireOp",EDGE,"E2.14.4.0"),sQuery(id+"F0.wireOp",EDGE,"E2.14.5.0"),sQuery(id+"F0.wireOp",EDGE,"E2.14.6.0"),sQuery(id+"F0.wireOp",EDGE,"E2.14.7.0"),sQuery(id+"F0.wireOp",EDGE,"E2.14.8.0"),sQuery(id+"F0.wireOp",EDGE,"E2.14.9.0"),sQuery(id+"F0.wireOp",EDGE,"E2.14.10.0"),sQuery(id+"F0.wireOp",EDGE,"E2.14.11.0"),sQuery(id+"F0.wireOp",EDGE,"E2.14.12.0"),sQuery(id+"F0.wireOp",EDGE,"E2.14.13.0"),sQuery(id+"F0.wireOp",EDGE,"E2.14.14.0"),sQuery(id+"F0.wireOp",EDGE,"E2.14.15.0"),sQuery(id+"F0.wireOp",EDGE,"E2.15.0.0"),sQuery(id+"F0.wireOp",EDGE,"E2.15.1.0"),sQuery(id+"F0.wireOp",EDGE,"E2.15.2.0"),sQuery(id+"F0.wireOp",EDGE,"E2.15.3.0"),sQuery(id+"F0.wireOp",EDGE,"E2.15.4.0"),sQuery(id+"F0.wireOp",EDGE,"E2.15.5.0"),sQuery(id+"F0.wireOp",EDGE,"E2.15.6.0"),sQuery(id+"F0.wireOp",EDGE,"E2.15.7.0"),sQuery(id+"F0.wireOp",EDGE,"E2.15.8.0"),sQuery(id+"F0.wireOp",EDGE,"E2.15.9.0"),sQuery(id+"F0.wireOp",EDGE,"E2.15.10.0"),sQuery(id+"F0.wireOp",EDGE,"E2.15.11.0"),sQuery(id+"F0.wireOp",EDGE,"E2.15.12.0"),sQuery(id+"F0.wireOp",EDGE,"E2.15.13.0"),sQuery(id+"F0.wireOp",EDGE,"E2.15.14.0"),sQuery(id+"F0.wireOp",EDGE,"E2.15.15.0"),sQuery(id+"F0.wireOp",EDGE,"6f7ae5fc-1566-4385-bfb5-e6e9eca27b98.0.0.16"),sQuery(id+"F0.wireOp",EDGE,"6f7ae5fc-1566-4385-bfb5-e6e9eca27b98.0.1.16"),sQuery(id+"F0.wireOp",EDGE,"6f7ae5fc-1566-4385-bfb5-e6e9eca27b98.0.2.16"),sQuery(id+"F0.wireOp",EDGE,"6f7ae5fc-1566-4385-bfb5-e6e9eca27b98.0.3.16"),sQuery(id+"F0.wireOp",EDGE,"6f7ae5fc-1566-4385-bfb5-e6e9eca27b98.0.4.16"),sQuery(id+"F0.wireOp",EDGE,"6f7ae5fc-1566-4385-bfb5-e6e9eca27b98.0.5.16"),sQuery(id+"F0.wireOp",EDGE,"6f7ae5fc-1566-4385-bfb5-e6e9eca27b98.0.6.16"),sQuery(id+"F0.wireOp",EDGE,"6f7ae5fc-1566-4385-bfb5-e6e9eca27b98.0.7.16"),sQuery(id+"F0.wireOp",EDGE,"6f7ae5fc-1566-4385-bfb5-e6e9eca27b98.0.8.16"),sQuery(id+"F0.wireOp",EDGE,"6f7ae5fc-1566-4385-bfb5-e6e9eca27b98.0.9.16"),sQuery(id+"F0.wireOp",EDGE,"6f7ae5fc-1566-4385-bfb5-e6e9eca27b98.0.10.16"),sQuery(id+"F0.wireOp",EDGE,"6f7ae5fc-1566-4385-bfb5-e6e9eca27b98.0.11.16"),sQuery(id+"F0.wireOp",EDGE,"6f7ae5fc-1566-4385-bfb5-e6e9eca27b98.0.12.16"),sQuery(id+"F0.wireOp",EDGE,"6f7ae5fc-1566-4385-bfb5-e6e9eca27b98.0.13.16"),sQuery(id+"F0.wireOp",EDGE,"6f7ae5fc-1566-4385-bfb5-e6e9eca27b98.0.14.16"),sQuery(id+"F0.wireOp",EDGE,"6f7ae5fc-1566-4385-bfb5-e6e9eca27b98.0.15.16"),sQuery(id+"F0.wireOp",EDGE,"da7dbd3b-79dd-422c-88db-b753358300f9.0.16.0"),sQuery(id+"F0.wireOp",EDGE,"da7dbd3b-79dd-422c-88db-b753358300f9.0.16.1"),sQuery(id+"F0.wireOp",EDGE,"da7dbd3b-79dd-422c-88db-b753358300f9.0.16.2"),sQuery(id+"F0.wireOp",EDGE,"da7dbd3b-79dd-422c-88db-b753358300f9.0.16.3"),sQuery(id+"F0.wireOp",EDGE,"da7dbd3b-79dd-422c-88db-b753358300f9.0.16.4"),sQuery(id+"F0.wireOp",EDGE,"da7dbd3b-79dd-422c-88db-b753358300f9.0.16.5"),sQuery(id+"F0.wireOp",EDGE,"da7dbd3b-79dd-422c-88db-b753358300f9.0.16.6"),sQuery(id+"F0.wireOp",EDGE,"da7dbd3b-79dd-422c-88db-b753358300f9.0.16.7"),sQuery(id+"F0.wireOp",EDGE,"da7dbd3b-79dd-422c-88db-b753358300f9.0.16.8"),sQuery(id+"F0.wireOp",EDGE,"da7dbd3b-79dd-422c-88db-b753358300f9.0.16.9"),sQuery(id+"F0.wireOp",EDGE,"da7dbd3b-79dd-422c-88db-b753358300f9.0.16.10"),sQuery(id+"F0.wireOp",EDGE,"da7dbd3b-79dd-422c-88db-b753358300f9.0.16.11"),sQuery(id+"F0.wireOp",EDGE,"da7dbd3b-79dd-422c-88db-b753358300f9.0.16.12"),sQuery(id+"F0.wireOp",EDGE,"da7dbd3b-79dd-422c-88db-b753358300f9.0.16.13"),sQuery(id+"F0.wireOp",EDGE,"da7dbd3b-79dd-422c-88db-b753358300f9.0.16.14"),sQuery(id+"F0.wireOp",EDGE,"da7dbd3b-79dd-422c-88db-b753358300f9.0.16.15"),sQuery(id+"F0.wireOp",EDGE,"da7dbd3b-79dd-422c-88db-b753358300f9.0.16.16")])],"isStart":false});
            var sketch = newSketch(context, id + "F2", { "sketchPlane" : qUnion([Q0])});
            skLineSegment(sketch, "E4.bottom", {"start": v(-80.75, 95) * mm, "end": v(-79.25, 95) * mm});
            skLineSegment(sketch, "E4.left", {"start": v(-80.75, 95) * mm, "end": v(-80.75, -83.75) * mm});
            skLineSegment(sketch, "E4.right", {"start": v(-79.25, 95) * mm, "end": v(-79.25, -82.25) * mm});
            skLineSegment(sketch, "E5.bottom", {"start": v(95, -82.25) * mm, "end": v(-79.25, -82.25) * mm});
            skLineSegment(sketch, "E5.top", {"start": v(95, -83.75) * mm, "end": v(-80.75, -83.75) * mm});
            skLineSegment(sketch, "E5.left", {"start": v(95, -82.25) * mm, "end": v(95, -83.75) * mm});
            skSolve(sketch);
        }
        {
            var Q0;
            {var subQ0=sQuery(id+"F0.wireOp",EDGE,"E3.0.1.16");var subQ1=sQuery(id+"F0.wireOp",EDGE,"6f7ae5fc-1566-4385-bfb5-e6e9eca27b98.0.0.16");var subQ2=sQuery(id+"F0.wireOp",EDGE,"E2.0.8.0");var subQ3=sQuery(id+"F0.wireOp",EDGE,"E2.0.9.0");var subQ4=sQuery(id+"F0.wireOp",EDGE,"E2.0.15.0");var subQ5=sQuery(id+"F0.wireOp",EDGE,"E2.0.14.0");var subQ6=sQuery(id+"F0.wireOp",EDGE,"E2.0.6.0");var subQ7=sQuery(id+"F0.wireOp",EDGE,"E3.0.6.16");var subQ8=sQuery(id+"F0.wireOp",EDGE,"E3.0.9.16");var subQ9=sQuery(id+"F0.wireOp",EDGE,"E2.0.13.0");var subQ10=sQuery(id+"F0.wireOp",EDGE,"E2.0.11.0");var subQ11=sQuery(id+"F0.wireOp",EDGE,"E3.0.14.16");var subQ12=sQuery(id+"F0.wireOp",EDGE,"E2.0.7.0");var subQ13=sQuery(id+"F0.wireOp",EDGE,"E0.right");var subQ14=sQuery(id+"F0.wireOp",EDGE,"E3.0.8.16");var subQ15=sQuery(id+"F0.wireOp",EDGE,"E0.left");var subQ16=sQuery(id+"F0.wireOp",EDGE,"E0.top");var subQ17=sQuery(id+"F0.wireOp",EDGE,"E2.0.4.0");var subQ18=sQuery(id+"F0.wireOp",EDGE,"E2.0.12.0");var subQ19=sQuery(id+"F0.wireOp",EDGE,"E0.bottom");var subQ20=sQuery(id+"F0.wireOp",EDGE,"E1");var subQ21=sQuery(id+"F0.wireOp",EDGE,"E3.0.10.16");var subQ22=sQuery(id+"F0.wireOp",EDGE,"E2.0.1.0");var subQ23=sQuery(id+"F0.wireOp",EDGE,"E2.0.2.0");var subQ24=sQuery(id+"F0.wireOp",EDGE,"E2.0.10.0");var subQ25=sQuery(id+"F0.wireOp",EDGE,"E2.0.3.0");var subQ26=sQuery(id+"F0.wireOp",EDGE,"E3.0.2.16");var subQ27=sQuery(id+"F0.wireOp",EDGE,"E2.0.5.0");var subQ28=sQuery(id+"F0.wireOp",EDGE,"E3.0.3.16");var subQ29=sQuery(id+"F0.wireOp",EDGE,"E3.0.4.16");var subQ30=sQuery(id+"F0.wireOp",EDGE,"E3.0.5.16");var subQ31=sQuery(id+"F0.wireOp",EDGE,"E3.0.7.16");var subQ32=sQuery(id+"F0.wireOp",EDGE,"E3.0.11.16");var subQ33=sQuery(id+"F0.wireOp",EDGE,"E3.0.12.16");var subQ34=sQuery(id+"F0.wireOp",EDGE,"E3.0.13.16");var subQ35=sQuery(id+"F0.wireOp",EDGE,"E3.0.15.16");var subQ36=sQuery(id+"F0.wireOp",EDGE,"E3.0.16.16");Q0=makeQuery(id+"FJqtpdUANZnq3Um_1.boolean.opBoolean","SPLIT",FACE,{"disambiguationData":[TD([makeQuery(id+"F1.opExtrude","SWEPT_FACE",FACE,{"disambiguationData":[OSD([subQ19])]})])],"derivedFrom":makeQuery(id+"F1.opExtrude","CAP_FACE",FACE,{"disambiguationData":[OSD([subQ19,subQ16,subQ15,subQ13,subQ20,subQ22,subQ23,subQ25,subQ17,subQ27,subQ6,subQ12,subQ2,subQ3,subQ24,subQ10,subQ18,subQ9,subQ5,subQ4,subQ1,sQuery(id+"F0.wireOp",EDGE,"E3.0.1.0"),sQuery(id+"F0.wireOp",EDGE,"E3.0.1.1"),sQuery(id+"F0.wireOp",EDGE,"E3.0.1.2"),sQuery(id+"F0.wireOp",EDGE,"E3.0.1.3"),sQuery(id+"F0.wireOp",EDGE,"E3.0.1.4"),sQuery(id+"F0.wireOp",EDGE,"E3.0.1.5"),sQuery(id+"F0.wireOp",EDGE,"E3.0.1.6"),sQuery(id+"F0.wireOp",EDGE,"E3.0.1.7"),sQuery(id+"F0.wireOp",EDGE,"E3.0.1.8"),sQuery(id+"F0.wireOp",EDGE,"E3.0.1.9"),sQuery(id+"F0.wireOp",EDGE,"E3.0.1.10"),sQuery(id+"F0.wireOp",EDGE,"E3.0.1.11"),sQuery(id+"F0.wireOp",EDGE,"E3.0.1.12"),sQuery(id+"F0.wireOp",EDGE,"E3.0.1.13"),sQuery(id+"F0.wireOp",EDGE,"E3.0.1.14"),sQuery(id+"F0.wireOp",EDGE,"E3.0.1.15"),subQ0,sQuery(id+"F0.wireOp",EDGE,"E3.0.2.0"),sQuery(id+"F0.wireOp",EDGE,"E3.0.2.1"),sQuery(id+"F0.wireOp",EDGE,"E3.0.2.2"),sQuery(id+"F0.wireOp",EDGE,"E3.0.2.3"),sQuery(id+"F0.wireOp",EDGE,"E3.0.2.4"),sQuery(id+"F0.wireOp",EDGE,"E3.0.2.5"),sQuery(id+"F0.wireOp",EDGE,"E3.0.2.6"),sQuery(id+"F0.wireOp",EDGE,"E3.0.2.7"),sQuery(id+"F0.wireOp",EDGE,"E3.0.2.8"),sQuery(id+"F0.wireOp",EDGE,"E3.0.2.9"),sQuery(id+"F0.wireOp",EDGE,"E3.0.2.10"),sQuery(id+"F0.wireOp",EDGE,"E3.0.2.11"),sQuery(id+"F0.wireOp",EDGE,"E3.0.2.12"),sQuery(id+"F0.wireOp",EDGE,"E3.0.2.13"),sQuery(id+"F0.wireOp",EDGE,"E3.0.2.14"),sQuery(id+"F0.wireOp",EDGE,"E3.0.2.15"),subQ26,sQuery(id+"F0.wireOp",EDGE,"E3.0.3.0"),sQuery(id+"F0.wireOp",EDGE,"E3.0.3.1"),sQuery(id+"F0.wireOp",EDGE,"E3.0.3.2"),sQuery(id+"F0.wireOp",EDGE,"E3.0.3.3"),sQuery(id+"F0.wireOp",EDGE,"E3.0.3.4"),sQuery(id+"F0.wireOp",EDGE,"E3.0.3.5"),sQuery(id+"F0.wireOp",EDGE,"E3.0.3.6"),sQuery(id+"F0.wireOp",EDGE,"E3.0.3.7"),sQuery(id+"F0.wireOp",EDGE,"E3.0.3.8"),sQuery(id+"F0.wireOp",EDGE,"E3.0.3.9"),sQuery(id+"F0.wireOp",EDGE,"E3.0.3.10"),sQuery(id+"F0.wireOp",EDGE,"E3.0.3.11"),sQuery(id+"F0.wireOp",EDGE,"E3.0.3.12"),sQuery(id+"F0.wireOp",EDGE,"E3.0.3.13"),sQuery(id+"F0.wireOp",EDGE,"E3.0.3.14"),sQuery(id+"F0.wireOp",EDGE,"E3.0.3.15"),subQ28,sQuery(id+"F0.wireOp",EDGE,"E3.0.4.0"),sQuery(id+"F0.wireOp",EDGE,"E3.0.4.1"),sQuery(id+"F0.wireOp",EDGE,"E3.0.4.2"),sQuery(id+"F0.wireOp",EDGE,"E3.0.4.3"),sQuery(id+"F0.wireOp",EDGE,"E3.0.4.4"),sQuery(id+"F0.wireOp",EDGE,"E3.0.4.5"),sQuery(id+"F0.wireOp",EDGE,"E3.0.4.6"),sQuery(id+"F0.wireOp",EDGE,"E3.0.4.7"),sQuery(id+"F0.wireOp",EDGE,"E3.0.4.8"),sQuery(id+"F0.wireOp",EDGE,"E3.0.4.9"),sQuery(id+"F0.wireOp",EDGE,"E3.0.4.10"),sQuery(id+"F0.wireOp",EDGE,"E3.0.4.11"),sQuery(id+"F0.wireOp",EDGE,"E3.0.4.12"),sQuery(id+"F0.wireOp",EDGE,"E3.0.4.13"),sQuery(id+"F0.wireOp",EDGE,"E3.0.4.14"),sQuery(id+"F0.wireOp",EDGE,"E3.0.4.15"),subQ29,sQuery(id+"F0.wireOp",EDGE,"E3.0.5.0"),sQuery(id+"F0.wireOp",EDGE,"E3.0.5.1"),sQuery(id+"F0.wireOp",EDGE,"E3.0.5.2"),sQuery(id+"F0.wireOp",EDGE,"E3.0.5.3"),sQuery(id+"F0.wireOp",EDGE,"E3.0.5.4"),sQuery(id+"F0.wireOp",EDGE,"E3.0.5.5"),sQuery(id+"F0.wireOp",EDGE,"E3.0.5.6"),sQuery(id+"F0.wireOp",EDGE,"E3.0.5.7"),sQuery(id+"F0.wireOp",EDGE,"E3.0.5.8"),sQuery(id+"F0.wireOp",EDGE,"E3.0.5.9"),sQuery(id+"F0.wireOp",EDGE,"E3.0.5.10"),sQuery(id+"F0.wireOp",EDGE,"E3.0.5.11"),sQuery(id+"F0.wireOp",EDGE,"E3.0.5.12"),sQuery(id+"F0.wireOp",EDGE,"E3.0.5.13"),sQuery(id+"F0.wireOp",EDGE,"E3.0.5.14"),sQuery(id+"F0.wireOp",EDGE,"E3.0.5.15"),subQ30,sQuery(id+"F0.wireOp",EDGE,"E3.0.6.0"),sQuery(id+"F0.wireOp",EDGE,"E3.0.6.1"),sQuery(id+"F0.wireOp",EDGE,"E3.0.6.2"),sQuery(id+"F0.wireOp",EDGE,"E3.0.6.3"),sQuery(id+"F0.wireOp",EDGE,"E3.0.6.4"),sQuery(id+"F0.wireOp",EDGE,"E3.0.6.5"),sQuery(id+"F0.wireOp",EDGE,"E3.0.6.6"),sQuery(id+"F0.wireOp",EDGE,"E3.0.6.7"),sQuery(id+"F0.wireOp",EDGE,"E3.0.6.8"),sQuery(id+"F0.wireOp",EDGE,"E3.0.6.9"),sQuery(id+"F0.wireOp",EDGE,"E3.0.6.10"),sQuery(id+"F0.wireOp",EDGE,"E3.0.6.11"),sQuery(id+"F0.wireOp",EDGE,"E3.0.6.12"),sQuery(id+"F0.wireOp",EDGE,"E3.0.6.13"),sQuery(id+"F0.wireOp",EDGE,"E3.0.6.14"),sQuery(id+"F0.wireOp",EDGE,"E3.0.6.15"),subQ7,sQuery(id+"F0.wireOp",EDGE,"E3.0.7.0"),sQuery(id+"F0.wireOp",EDGE,"E3.0.7.1"),sQuery(id+"F0.wireOp",EDGE,"E3.0.7.2"),sQuery(id+"F0.wireOp",EDGE,"E3.0.7.3"),sQuery(id+"F0.wireOp",EDGE,"E3.0.7.4"),sQuery(id+"F0.wireOp",EDGE,"E3.0.7.5"),sQuery(id+"F0.wireOp",EDGE,"E3.0.7.6"),sQuery(id+"F0.wireOp",EDGE,"E3.0.7.7"),sQuery(id+"F0.wireOp",EDGE,"E3.0.7.8"),sQuery(id+"F0.wireOp",EDGE,"E3.0.7.9"),sQuery(id+"F0.wireOp",EDGE,"E3.0.7.10"),sQuery(id+"F0.wireOp",EDGE,"E3.0.7.11"),sQuery(id+"F0.wireOp",EDGE,"E3.0.7.12"),sQuery(id+"F0.wireOp",EDGE,"E3.0.7.13"),sQuery(id+"F0.wireOp",EDGE,"E3.0.7.14"),sQuery(id+"F0.wireOp",EDGE,"E3.0.7.15"),subQ31,sQuery(id+"F0.wireOp",EDGE,"E3.0.8.0"),sQuery(id+"F0.wireOp",EDGE,"E3.0.8.1"),sQuery(id+"F0.wireOp",EDGE,"E3.0.8.2"),sQuery(id+"F0.wireOp",EDGE,"E3.0.8.3"),sQuery(id+"F0.wireOp",EDGE,"E3.0.8.4"),sQuery(id+"F0.wireOp",EDGE,"E3.0.8.5"),sQuery(id+"F0.wireOp",EDGE,"E3.0.8.6"),sQuery(id+"F0.wireOp",EDGE,"E3.0.8.7"),sQuery(id+"F0.wireOp",EDGE,"E3.0.8.8"),sQuery(id+"F0.wireOp",EDGE,"E3.0.8.9"),sQuery(id+"F0.wireOp",EDGE,"E3.0.8.10"),sQuery(id+"F0.wireOp",EDGE,"E3.0.8.11"),sQuery(id+"F0.wireOp",EDGE,"E3.0.8.12"),sQuery(id+"F0.wireOp",EDGE,"E3.0.8.13"),sQuery(id+"F0.wireOp",EDGE,"E3.0.8.14"),sQuery(id+"F0.wireOp",EDGE,"E3.0.8.15"),subQ14,sQuery(id+"F0.wireOp",EDGE,"E3.0.9.0"),sQuery(id+"F0.wireOp",EDGE,"E3.0.9.1"),sQuery(id+"F0.wireOp",EDGE,"E3.0.9.2"),sQuery(id+"F0.wireOp",EDGE,"E3.0.9.3"),sQuery(id+"F0.wireOp",EDGE,"E3.0.9.4"),sQuery(id+"F0.wireOp",EDGE,"E3.0.9.5"),sQuery(id+"F0.wireOp",EDGE,"E3.0.9.6"),sQuery(id+"F0.wireOp",EDGE,"E3.0.9.7"),sQuery(id+"F0.wireOp",EDGE,"E3.0.9.8"),sQuery(id+"F0.wireOp",EDGE,"E3.0.9.9"),sQuery(id+"F0.wireOp",EDGE,"E3.0.9.10"),sQuery(id+"F0.wireOp",EDGE,"E3.0.9.11"),sQuery(id+"F0.wireOp",EDGE,"E3.0.9.12"),sQuery(id+"F0.wireOp",EDGE,"E3.0.9.13"),sQuery(id+"F0.wireOp",EDGE,"E3.0.9.14"),sQuery(id+"F0.wireOp",EDGE,"E3.0.9.15"),subQ8,sQuery(id+"F0.wireOp",EDGE,"E3.0.10.0"),sQuery(id+"F0.wireOp",EDGE,"E3.0.10.1"),sQuery(id+"F0.wireOp",EDGE,"E3.0.10.2"),sQuery(id+"F0.wireOp",EDGE,"E3.0.10.3"),sQuery(id+"F0.wireOp",EDGE,"E3.0.10.4"),sQuery(id+"F0.wireOp",EDGE,"E3.0.10.5"),sQuery(id+"F0.wireOp",EDGE,"E3.0.10.6"),sQuery(id+"F0.wireOp",EDGE,"E3.0.10.7"),sQuery(id+"F0.wireOp",EDGE,"E3.0.10.8"),sQuery(id+"F0.wireOp",EDGE,"E3.0.10.9"),sQuery(id+"F0.wireOp",EDGE,"E3.0.10.10"),sQuery(id+"F0.wireOp",EDGE,"E3.0.10.11"),sQuery(id+"F0.wireOp",EDGE,"E3.0.10.12"),sQuery(id+"F0.wireOp",EDGE,"E3.0.10.13"),sQuery(id+"F0.wireOp",EDGE,"E3.0.10.14"),sQuery(id+"F0.wireOp",EDGE,"E3.0.10.15"),subQ21,sQuery(id+"F0.wireOp",EDGE,"E3.0.11.0"),sQuery(id+"F0.wireOp",EDGE,"E3.0.11.1"),sQuery(id+"F0.wireOp",EDGE,"E3.0.11.2"),sQuery(id+"F0.wireOp",EDGE,"E3.0.11.3"),sQuery(id+"F0.wireOp",EDGE,"E3.0.11.4"),sQuery(id+"F0.wireOp",EDGE,"E3.0.11.5"),sQuery(id+"F0.wireOp",EDGE,"E3.0.11.6"),sQuery(id+"F0.wireOp",EDGE,"E3.0.11.7"),sQuery(id+"F0.wireOp",EDGE,"E3.0.11.8"),sQuery(id+"F0.wireOp",EDGE,"E3.0.11.9"),sQuery(id+"F0.wireOp",EDGE,"E3.0.11.10"),sQuery(id+"F0.wireOp",EDGE,"E3.0.11.11"),sQuery(id+"F0.wireOp",EDGE,"E3.0.11.12"),sQuery(id+"F0.wireOp",EDGE,"E3.0.11.13"),sQuery(id+"F0.wireOp",EDGE,"E3.0.11.14"),sQuery(id+"F0.wireOp",EDGE,"E3.0.11.15"),subQ32,sQuery(id+"F0.wireOp",EDGE,"E3.0.12.0"),sQuery(id+"F0.wireOp",EDGE,"E3.0.12.1"),sQuery(id+"F0.wireOp",EDGE,"E3.0.12.2"),sQuery(id+"F0.wireOp",EDGE,"E3.0.12.3"),sQuery(id+"F0.wireOp",EDGE,"E3.0.12.4"),sQuery(id+"F0.wireOp",EDGE,"E3.0.12.5"),sQuery(id+"F0.wireOp",EDGE,"E3.0.12.6"),sQuery(id+"F0.wireOp",EDGE,"E3.0.12.7"),sQuery(id+"F0.wireOp",EDGE,"E3.0.12.8"),sQuery(id+"F0.wireOp",EDGE,"E3.0.12.9"),sQuery(id+"F0.wireOp",EDGE,"E3.0.12.10"),sQuery(id+"F0.wireOp",EDGE,"E3.0.12.11"),sQuery(id+"F0.wireOp",EDGE,"E3.0.12.12"),sQuery(id+"F0.wireOp",EDGE,"E3.0.12.13"),sQuery(id+"F0.wireOp",EDGE,"E3.0.12.14"),sQuery(id+"F0.wireOp",EDGE,"E3.0.12.15"),subQ33,sQuery(id+"F0.wireOp",EDGE,"E3.0.13.0"),sQuery(id+"F0.wireOp",EDGE,"E3.0.13.1"),sQuery(id+"F0.wireOp",EDGE,"E3.0.13.2"),sQuery(id+"F0.wireOp",EDGE,"E3.0.13.3"),sQuery(id+"F0.wireOp",EDGE,"E3.0.13.4"),sQuery(id+"F0.wireOp",EDGE,"E3.0.13.5"),sQuery(id+"F0.wireOp",EDGE,"E3.0.13.6"),sQuery(id+"F0.wireOp",EDGE,"E3.0.13.7"),sQuery(id+"F0.wireOp",EDGE,"E3.0.13.8"),sQuery(id+"F0.wireOp",EDGE,"E3.0.13.9"),sQuery(id+"F0.wireOp",EDGE,"E3.0.13.10"),sQuery(id+"F0.wireOp",EDGE,"E3.0.13.11"),sQuery(id+"F0.wireOp",EDGE,"E3.0.13.12"),sQuery(id+"F0.wireOp",EDGE,"E3.0.13.13"),sQuery(id+"F0.wireOp",EDGE,"E3.0.13.14"),sQuery(id+"F0.wireOp",EDGE,"E3.0.13.15"),subQ34,sQuery(id+"F0.wireOp",EDGE,"E3.0.14.0"),sQuery(id+"F0.wireOp",EDGE,"E3.0.14.1"),sQuery(id+"F0.wireOp",EDGE,"E3.0.14.2"),sQuery(id+"F0.wireOp",EDGE,"E3.0.14.3"),sQuery(id+"F0.wireOp",EDGE,"E3.0.14.4"),sQuery(id+"F0.wireOp",EDGE,"E3.0.14.5"),sQuery(id+"F0.wireOp",EDGE,"E3.0.14.6"),sQuery(id+"F0.wireOp",EDGE,"E3.0.14.7"),sQuery(id+"F0.wireOp",EDGE,"E3.0.14.8"),sQuery(id+"F0.wireOp",EDGE,"E3.0.14.9"),sQuery(id+"F0.wireOp",EDGE,"E3.0.14.10"),sQuery(id+"F0.wireOp",EDGE,"E3.0.14.11"),sQuery(id+"F0.wireOp",EDGE,"E3.0.14.12"),sQuery(id+"F0.wireOp",EDGE,"E3.0.14.13"),sQuery(id+"F0.wireOp",EDGE,"E3.0.14.14"),sQuery(id+"F0.wireOp",EDGE,"E3.0.14.15"),subQ11,sQuery(id+"F0.wireOp",EDGE,"E3.0.15.0"),sQuery(id+"F0.wireOp",EDGE,"E3.0.15.1"),sQuery(id+"F0.wireOp",EDGE,"E3.0.15.2"),sQuery(id+"F0.wireOp",EDGE,"E3.0.15.3"),sQuery(id+"F0.wireOp",EDGE,"E3.0.15.4"),sQuery(id+"F0.wireOp",EDGE,"E3.0.15.5"),sQuery(id+"F0.wireOp",EDGE,"E3.0.15.6"),sQuery(id+"F0.wireOp",EDGE,"E3.0.15.7"),sQuery(id+"F0.wireOp",EDGE,"E3.0.15.8"),sQuery(id+"F0.wireOp",EDGE,"E3.0.15.9"),sQuery(id+"F0.wireOp",EDGE,"E3.0.15.10"),sQuery(id+"F0.wireOp",EDGE,"E3.0.15.11"),sQuery(id+"F0.wireOp",EDGE,"E3.0.15.12"),sQuery(id+"F0.wireOp",EDGE,"E3.0.15.13"),sQuery(id+"F0.wireOp",EDGE,"E3.0.15.14"),sQuery(id+"F0.wireOp",EDGE,"E3.0.15.15"),subQ35,sQuery(id+"F0.wireOp",EDGE,"E3.0.16.0"),sQuery(id+"F0.wireOp",EDGE,"E3.0.16.1"),sQuery(id+"F0.wireOp",EDGE,"E3.0.16.2"),sQuery(id+"F0.wireOp",EDGE,"E3.0.16.3"),sQuery(id+"F0.wireOp",EDGE,"E3.0.16.4"),sQuery(id+"F0.wireOp",EDGE,"E3.0.16.5"),sQuery(id+"F0.wireOp",EDGE,"E3.0.16.6"),sQuery(id+"F0.wireOp",EDGE,"E3.0.16.7"),sQuery(id+"F0.wireOp",EDGE,"E3.0.16.8"),sQuery(id+"F0.wireOp",EDGE,"E3.0.16.9"),sQuery(id+"F0.wireOp",EDGE,"E3.0.16.10"),sQuery(id+"F0.wireOp",EDGE,"E3.0.16.11"),sQuery(id+"F0.wireOp",EDGE,"E3.0.16.12"),sQuery(id+"F0.wireOp",EDGE,"E3.0.16.13"),sQuery(id+"F0.wireOp",EDGE,"E3.0.16.14"),sQuery(id+"F0.wireOp",EDGE,"E3.0.16.15"),subQ36])],"isStart":false})});}
            var sketch = newSketch(context, id + "F3", { "sketchPlane" : qUnion([Q0])});
            skLineSegment(sketch, "E6.bottom", {"start": v(-68.75, -83) * mm, "end": v(-67.25, -83) * mm});
            skLineSegment(sketch, "E6.top", {"start": v(-68.75, -89) * mm, "end": v(-67.25, -89) * mm});
            skLineSegment(sketch, "E6.left", {"start": v(-68.75, -83) * mm, "end": v(-68.75, -89) * mm});
            skLineSegment(sketch, "E6.right", {"start": v(-67.25, -83) * mm, "end": v(-67.25, -89) * mm});
            skLineSegment(sketch, "E7.1.0.0", {"start": v(-56.75, -83) * mm, "end": v(-56.75, -89) * mm});
            skLineSegment(sketch, "E7.1.0.1", {"start": v(-56.75, -83) * mm, "end": v(-55.25, -83) * mm});
            skLineSegment(sketch, "E7.1.0.2", {"start": v(-55.25, -83) * mm, "end": v(-55.25, -89) * mm});
            skLineSegment(sketch, "E7.1.0.3", {"start": v(-56.75, -89) * mm, "end": v(-55.25, -89) * mm});
            skLineSegment(sketch, "E7.2.0.0", {"start": v(-44.75, -83) * mm, "end": v(-44.75, -89) * mm});
            skLineSegment(sketch, "E7.2.0.1", {"start": v(-44.75, -83) * mm, "end": v(-43.25, -83) * mm});
            skLineSegment(sketch, "E7.2.0.2", {"start": v(-43.25, -83) * mm, "end": v(-43.25, -89) * mm});
            skLineSegment(sketch, "E7.2.0.3", {"start": v(-44.75, -89) * mm, "end": v(-43.25, -89) * mm});
            skLineSegment(sketch, "E7.3.0.0", {"start": v(-32.75, -83) * mm, "end": v(-32.75, -89) * mm});
            skLineSegment(sketch, "E7.3.0.1", {"start": v(-32.75, -83) * mm, "end": v(-31.25, -83) * mm});
            skLineSegment(sketch, "E7.3.0.2", {"start": v(-31.25, -83) * mm, "end": v(-31.25, -89) * mm});
            skLineSegment(sketch, "E7.3.0.3", {"start": v(-32.75, -89) * mm, "end": v(-31.25, -89) * mm});
            skLineSegment(sketch, "E7.4.0.0", {"start": v(-20.75, -83) * mm, "end": v(-20.75, -89) * mm});
            skLineSegment(sketch, "E7.4.0.1", {"start": v(-20.75, -83) * mm, "end": v(-19.25, -83) * mm});
            skLineSegment(sketch, "E7.4.0.2", {"start": v(-19.25, -83) * mm, "end": v(-19.25, -89) * mm});
            skLineSegment(sketch, "E7.4.0.3", {"start": v(-20.75, -89) * mm, "end": v(-19.25, -89) * mm});
            skLineSegment(sketch, "E7.5.0.0", {"start": v(-8.75, -83) * mm, "end": v(-8.75, -89) * mm});
            skLineSegment(sketch, "E7.5.0.1", {"start": v(-8.75, -83) * mm, "end": v(-7.25, -83) * mm});
            skLineSegment(sketch, "E7.5.0.2", {"start": v(-7.25, -83) * mm, "end": v(-7.25, -89) * mm});
            skLineSegment(sketch, "E7.5.0.3", {"start": v(-8.75, -89) * mm, "end": v(-7.25, -89) * mm});
            skLineSegment(sketch, "E7.6.0.0", {"start": v(3.25, -83) * mm, "end": v(3.25, -89) * mm});
            skLineSegment(sketch, "E7.6.0.1", {"start": v(3.25, -83) * mm, "end": v(4.75, -83) * mm});
            skLineSegment(sketch, "E7.6.0.2", {"start": v(4.75, -83) * mm, "end": v(4.75, -89) * mm});
            skLineSegment(sketch, "E7.6.0.3", {"start": v(3.25, -89) * mm, "end": v(4.75, -89) * mm});
            skLineSegment(sketch, "E7.7.0.0", {"start": v(15.25, -83) * mm, "end": v(15.25, -89) * mm});
            skLineSegment(sketch, "E7.7.0.1", {"start": v(15.25, -83) * mm, "end": v(16.75, -83) * mm});
            skLineSegment(sketch, "E7.7.0.2", {"start": v(16.75, -83) * mm, "end": v(16.75, -89) * mm});
            skLineSegment(sketch, "E7.7.0.3", {"start": v(15.25, -89) * mm, "end": v(16.75, -89) * mm});
            skLineSegment(sketch, "E7.8.0.0", {"start": v(27.25, -83) * mm, "end": v(27.25, -89) * mm});
            skLineSegment(sketch, "E7.8.0.1", {"start": v(27.25, -83) * mm, "end": v(28.75, -83) * mm});
            skLineSegment(sketch, "E7.8.0.2", {"start": v(28.75, -83) * mm, "end": v(28.75, -89) * mm});
            skLineSegment(sketch, "E7.8.0.3", {"start": v(27.25, -89) * mm, "end": v(28.75, -89) * mm});
            skLineSegment(sketch, "E7.9.0.0", {"start": v(39.25, -83) * mm, "end": v(39.25, -89) * mm});
            skLineSegment(sketch, "E7.9.0.1", {"start": v(39.25, -83) * mm, "end": v(40.75, -83) * mm});
            skLineSegment(sketch, "E7.9.0.2", {"start": v(40.75, -83) * mm, "end": v(40.75, -89) * mm});
            skLineSegment(sketch, "E7.9.0.3", {"start": v(39.25, -89) * mm, "end": v(40.75, -89) * mm});
            skLineSegment(sketch, "E7.10.0.0", {"start": v(51.25, -83) * mm, "end": v(51.25, -89) * mm});
            skLineSegment(sketch, "E7.10.0.1", {"start": v(51.25, -83) * mm, "end": v(52.75, -83) * mm});
            skLineSegment(sketch, "E7.10.0.2", {"start": v(52.75, -83) * mm, "end": v(52.75, -89) * mm});
            skLineSegment(sketch, "E7.10.0.3", {"start": v(51.25, -89) * mm, "end": v(52.75, -89) * mm});
            skLineSegment(sketch, "E7.11.0.0", {"start": v(63.25, -83) * mm, "end": v(63.25, -89) * mm});
            skLineSegment(sketch, "E7.11.0.1", {"start": v(63.25, -83) * mm, "end": v(64.75, -83) * mm});
            skLineSegment(sketch, "E7.11.0.2", {"start": v(64.75, -83) * mm, "end": v(64.75, -89) * mm});
            skLineSegment(sketch, "E7.11.0.3", {"start": v(63.25, -89) * mm, "end": v(64.75, -89) * mm});
            skLineSegment(sketch, "E7.12.0.0", {"start": v(75.25, -83) * mm, "end": v(75.25, -89) * mm});
            skLineSegment(sketch, "E7.12.0.1", {"start": v(75.25, -83) * mm, "end": v(76.75, -83) * mm});
            skLineSegment(sketch, "E7.12.0.2", {"start": v(76.75, -83) * mm, "end": v(76.75, -89) * mm});
            skLineSegment(sketch, "E7.12.0.3", {"start": v(75.25, -89) * mm, "end": v(76.75, -89) * mm});
            skLineSegment(sketch, "E7.13.0.0", {"start": v(87.25, -83) * mm, "end": v(87.25, -89) * mm});
            skLineSegment(sketch, "E7.13.0.1", {"start": v(87.25, -83) * mm, "end": v(88.75, -83) * mm});
            skLineSegment(sketch, "E7.13.0.2", {"start": v(88.75, -83) * mm, "end": v(88.75, -89) * mm});
            skLineSegment(sketch, "E7.13.0.3", {"start": v(87.25, -89) * mm, "end": v(88.75, -89) * mm});
            skLineSegment(sketch, "E7.direction1", {"start": v(-68.75, -89) * mm, "end": v(-56.75, -89) * mm, "construction": true});
            skLineSegment(sketch, "E8.bottom", {"start": v(-80, -70.25) * mm, "end": v(-86, -70.25) * mm});
            skLineSegment(sketch, "E8.top", {"start": v(-80, -71.75) * mm, "end": v(-86, -71.75) * mm});
            skLineSegment(sketch, "E8.left", {"start": v(-80, -70.25) * mm, "end": v(-80, -71.75) * mm});
            skLineSegment(sketch, "E8.right", {"start": v(-86, -70.25) * mm, "end": v(-86, -71.75) * mm});
            skLineSegment(sketch, "E9.0.1.0", {"start": v(-86, -58.25) * mm, "end": v(-86, -59.75) * mm});
            skLineSegment(sketch, "E9.0.1.1", {"start": v(-80, -58.25) * mm, "end": v(-86, -58.25) * mm});
            skLineSegment(sketch, "E9.0.1.2", {"start": v(-80, -59.75) * mm, "end": v(-86, -59.75) * mm});
            skLineSegment(sketch, "E9.0.1.3", {"start": v(-80, -58.25) * mm, "end": v(-80, -59.75) * mm});
            skLineSegment(sketch, "E9.0.2.0", {"start": v(-86, -46.25) * mm, "end": v(-86, -47.75) * mm});
            skLineSegment(sketch, "E9.0.2.1", {"start": v(-80, -46.25) * mm, "end": v(-86, -46.25) * mm});
            skLineSegment(sketch, "E9.0.2.2", {"start": v(-80, -47.75) * mm, "end": v(-86, -47.75) * mm});
            skLineSegment(sketch, "E9.0.2.3", {"start": v(-80, -46.25) * mm, "end": v(-80, -47.75) * mm});
            skLineSegment(sketch, "E9.0.3.0", {"start": v(-86, -34.25) * mm, "end": v(-86, -35.75) * mm});
            skLineSegment(sketch, "E9.0.3.1", {"start": v(-80, -34.25) * mm, "end": v(-86, -34.25) * mm});
            skLineSegment(sketch, "E9.0.3.2", {"start": v(-80, -35.75) * mm, "end": v(-86, -35.75) * mm});
            skLineSegment(sketch, "E9.0.3.3", {"start": v(-80, -34.25) * mm, "end": v(-80, -35.75) * mm});
            skLineSegment(sketch, "E9.0.4.0", {"start": v(-86, -22.25) * mm, "end": v(-86, -23.75) * mm});
            skLineSegment(sketch, "E9.0.4.1", {"start": v(-80, -22.25) * mm, "end": v(-86, -22.25) * mm});
            skLineSegment(sketch, "E9.0.4.2", {"start": v(-80, -23.75) * mm, "end": v(-86, -23.75) * mm});
            skLineSegment(sketch, "E9.0.4.3", {"start": v(-80, -22.25) * mm, "end": v(-80, -23.75) * mm});
            skLineSegment(sketch, "E9.0.5.0", {"start": v(-86, -10.25) * mm, "end": v(-86, -11.75) * mm});
            skLineSegment(sketch, "E9.0.5.1", {"start": v(-80, -10.25) * mm, "end": v(-86, -10.25) * mm});
            skLineSegment(sketch, "E9.0.5.2", {"start": v(-80, -11.75) * mm, "end": v(-86, -11.75) * mm});
            skLineSegment(sketch, "E9.0.5.3", {"start": v(-80, -10.25) * mm, "end": v(-80, -11.75) * mm});
            skLineSegment(sketch, "E9.0.6.0", {"start": v(-86, 1.75) * mm, "end": v(-86, 0.25) * mm});
            skLineSegment(sketch, "E9.0.6.1", {"start": v(-80, 1.75) * mm, "end": v(-86, 1.75) * mm});
            skLineSegment(sketch, "E9.0.6.2", {"start": v(-80, 0.25) * mm, "end": v(-86, 0.25) * mm});
            skLineSegment(sketch, "E9.0.6.3", {"start": v(-80, 1.75) * mm, "end": v(-80, 0.25) * mm});
            skLineSegment(sketch, "E9.0.7.0", {"start": v(-86, 13.75) * mm, "end": v(-86, 12.25) * mm});
            skLineSegment(sketch, "E9.0.7.1", {"start": v(-80, 13.75) * mm, "end": v(-86, 13.75) * mm});
            skLineSegment(sketch, "E9.0.7.2", {"start": v(-80, 12.25) * mm, "end": v(-86, 12.25) * mm});
            skLineSegment(sketch, "E9.0.7.3", {"start": v(-80, 13.75) * mm, "end": v(-80, 12.25) * mm});
            skLineSegment(sketch, "E9.0.8.0", {"start": v(-86, 25.75) * mm, "end": v(-86, 24.25) * mm});
            skLineSegment(sketch, "E9.0.8.1", {"start": v(-80, 25.75) * mm, "end": v(-86, 25.75) * mm});
            skLineSegment(sketch, "E9.0.8.2", {"start": v(-80, 24.25) * mm, "end": v(-86, 24.25) * mm});
            skLineSegment(sketch, "E9.0.8.3", {"start": v(-80, 25.75) * mm, "end": v(-80, 24.25) * mm});
            skLineSegment(sketch, "E9.0.9.0", {"start": v(-86, 37.75) * mm, "end": v(-86, 36.25) * mm});
            skLineSegment(sketch, "E9.0.9.1", {"start": v(-80, 37.75) * mm, "end": v(-86, 37.75) * mm});
            skLineSegment(sketch, "E9.0.9.2", {"start": v(-80, 36.25) * mm, "end": v(-86, 36.25) * mm});
            skLineSegment(sketch, "E9.0.9.3", {"start": v(-80, 37.75) * mm, "end": v(-80, 36.25) * mm});
            skLineSegment(sketch, "E9.0.10.0", {"start": v(-86, 49.75) * mm, "end": v(-86, 48.25) * mm});
            skLineSegment(sketch, "E9.0.10.1", {"start": v(-80, 49.75) * mm, "end": v(-86, 49.75) * mm});
            skLineSegment(sketch, "E9.0.10.2", {"start": v(-80, 48.25) * mm, "end": v(-86, 48.25) * mm});
            skLineSegment(sketch, "E9.0.10.3", {"start": v(-80, 49.75) * mm, "end": v(-80, 48.25) * mm});
            skLineSegment(sketch, "E9.0.11.0", {"start": v(-86, 61.75) * mm, "end": v(-86, 60.25) * mm});
            skLineSegment(sketch, "E9.0.11.1", {"start": v(-80, 61.75) * mm, "end": v(-86, 61.75) * mm});
            skLineSegment(sketch, "E9.0.11.2", {"start": v(-80, 60.25) * mm, "end": v(-86, 60.25) * mm});
            skLineSegment(sketch, "E9.0.11.3", {"start": v(-80, 61.75) * mm, "end": v(-80, 60.25) * mm});
            skLineSegment(sketch, "E9.0.12.0", {"start": v(-86, 73.75) * mm, "end": v(-86, 72.25) * mm});
            skLineSegment(sketch, "E9.0.12.1", {"start": v(-80, 73.75) * mm, "end": v(-86, 73.75) * mm});
            skLineSegment(sketch, "E9.0.12.2", {"start": v(-80, 72.25) * mm, "end": v(-86, 72.25) * mm});
            skLineSegment(sketch, "E9.0.12.3", {"start": v(-80, 73.75) * mm, "end": v(-80, 72.25) * mm});
            skLineSegment(sketch, "E9.0.13.0", {"start": v(-86, 85.75) * mm, "end": v(-86, 84.25) * mm});
            skLineSegment(sketch, "E9.0.13.1", {"start": v(-80, 85.75) * mm, "end": v(-86, 85.75) * mm});
            skLineSegment(sketch, "E9.0.13.2", {"start": v(-80, 84.25) * mm, "end": v(-86, 84.25) * mm});
            skLineSegment(sketch, "E9.0.13.3", {"start": v(-80, 85.75) * mm, "end": v(-80, 84.25) * mm});
            skLineSegment(sketch, "E9.direction1", {"start": v(-86, -71.75) * mm, "end": v(-57.74, -71.75) * mm, "construction": true});
            skLineSegment(sketch, "E9.direction2", {"start": v(-86, -71.75) * mm, "end": v(-86, -59.75) * mm, "construction": true});
            skSolve(sketch);
        }
        {
            var Q0;
            {var subQ0=sQuery(id+"F0.wireOp",EDGE,"E3.0.1.16");var subQ1=sQuery(id+"F0.wireOp",EDGE,"6f7ae5fc-1566-4385-bfb5-e6e9eca27b98.0.0.16");var subQ2=sQuery(id+"F0.wireOp",EDGE,"E2.0.8.0");var subQ3=sQuery(id+"F0.wireOp",EDGE,"E2.0.9.0");var subQ4=sQuery(id+"F0.wireOp",EDGE,"E2.0.15.0");var subQ5=sQuery(id+"F0.wireOp",EDGE,"E2.0.14.0");var subQ6=sQuery(id+"F0.wireOp",EDGE,"E2.0.6.0");var subQ7=sQuery(id+"F0.wireOp",EDGE,"E3.0.6.16");var subQ8=sQuery(id+"F0.wireOp",EDGE,"E3.0.9.16");var subQ9=sQuery(id+"F0.wireOp",EDGE,"E2.0.13.0");var subQ10=sQuery(id+"F0.wireOp",EDGE,"E2.0.11.0");var subQ11=sQuery(id+"F0.wireOp",EDGE,"E3.0.14.16");var subQ12=sQuery(id+"F0.wireOp",EDGE,"E2.0.7.0");var subQ13=sQuery(id+"F0.wireOp",EDGE,"E0.right");var subQ14=sQuery(id+"F0.wireOp",EDGE,"E3.0.8.16");var subQ15=sQuery(id+"F0.wireOp",EDGE,"E0.left");var subQ16=sQuery(id+"F0.wireOp",EDGE,"E0.top");var subQ17=sQuery(id+"F0.wireOp",EDGE,"E2.0.4.0");var subQ18=sQuery(id+"F0.wireOp",EDGE,"E2.0.12.0");var subQ19=sQuery(id+"F0.wireOp",EDGE,"E0.bottom");var subQ20=sQuery(id+"F0.wireOp",EDGE,"E1");var subQ21=sQuery(id+"F0.wireOp",EDGE,"E3.0.10.16");var subQ22=sQuery(id+"F0.wireOp",EDGE,"E2.0.1.0");var subQ23=sQuery(id+"F0.wireOp",EDGE,"E2.0.2.0");var subQ24=sQuery(id+"F0.wireOp",EDGE,"E2.0.10.0");var subQ25=sQuery(id+"F0.wireOp",EDGE,"E2.0.3.0");var subQ26=sQuery(id+"F0.wireOp",EDGE,"E3.0.2.16");var subQ27=sQuery(id+"F0.wireOp",EDGE,"E2.0.5.0");var subQ28=sQuery(id+"F0.wireOp",EDGE,"E3.0.3.16");var subQ29=sQuery(id+"F0.wireOp",EDGE,"E3.0.4.16");var subQ30=sQuery(id+"F0.wireOp",EDGE,"E3.0.5.16");var subQ31=sQuery(id+"F0.wireOp",EDGE,"E3.0.7.16");var subQ32=sQuery(id+"F0.wireOp",EDGE,"E3.0.11.16");var subQ33=sQuery(id+"F0.wireOp",EDGE,"E3.0.12.16");var subQ34=sQuery(id+"F0.wireOp",EDGE,"E3.0.13.16");var subQ35=sQuery(id+"F0.wireOp",EDGE,"E3.0.15.16");var subQ36=sQuery(id+"F0.wireOp",EDGE,"E3.0.16.16");Q0=makeQuery(id+"FJqtpdUANZnq3Um_1.boolean.opBoolean","SPLIT",FACE,{"disambiguationData":[TD([makeQuery(id+"F1.opExtrude","SWEPT_FACE",FACE,{"disambiguationData":[OSD([subQ19])]})])],"derivedFrom":makeQuery(id+"F1.opExtrude","CAP_FACE",FACE,{"disambiguationData":[OSD([subQ19,subQ16,subQ15,subQ13,subQ20,subQ22,subQ23,subQ25,subQ17,subQ27,subQ6,subQ12,subQ2,subQ3,subQ24,subQ10,subQ18,subQ9,subQ5,subQ4,subQ1,sQuery(id+"F0.wireOp",EDGE,"E3.0.1.0"),sQuery(id+"F0.wireOp",EDGE,"E3.0.1.1"),sQuery(id+"F0.wireOp",EDGE,"E3.0.1.2"),sQuery(id+"F0.wireOp",EDGE,"E3.0.1.3"),sQuery(id+"F0.wireOp",EDGE,"E3.0.1.4"),sQuery(id+"F0.wireOp",EDGE,"E3.0.1.5"),sQuery(id+"F0.wireOp",EDGE,"E3.0.1.6"),sQuery(id+"F0.wireOp",EDGE,"E3.0.1.7"),sQuery(id+"F0.wireOp",EDGE,"E3.0.1.8"),sQuery(id+"F0.wireOp",EDGE,"E3.0.1.9"),sQuery(id+"F0.wireOp",EDGE,"E3.0.1.10"),sQuery(id+"F0.wireOp",EDGE,"E3.0.1.11"),sQuery(id+"F0.wireOp",EDGE,"E3.0.1.12"),sQuery(id+"F0.wireOp",EDGE,"E3.0.1.13"),sQuery(id+"F0.wireOp",EDGE,"E3.0.1.14"),sQuery(id+"F0.wireOp",EDGE,"E3.0.1.15"),subQ0,sQuery(id+"F0.wireOp",EDGE,"E3.0.2.0"),sQuery(id+"F0.wireOp",EDGE,"E3.0.2.1"),sQuery(id+"F0.wireOp",EDGE,"E3.0.2.2"),sQuery(id+"F0.wireOp",EDGE,"E3.0.2.3"),sQuery(id+"F0.wireOp",EDGE,"E3.0.2.4"),sQuery(id+"F0.wireOp",EDGE,"E3.0.2.5"),sQuery(id+"F0.wireOp",EDGE,"E3.0.2.6"),sQuery(id+"F0.wireOp",EDGE,"E3.0.2.7"),sQuery(id+"F0.wireOp",EDGE,"E3.0.2.8"),sQuery(id+"F0.wireOp",EDGE,"E3.0.2.9"),sQuery(id+"F0.wireOp",EDGE,"E3.0.2.10"),sQuery(id+"F0.wireOp",EDGE,"E3.0.2.11"),sQuery(id+"F0.wireOp",EDGE,"E3.0.2.12"),sQuery(id+"F0.wireOp",EDGE,"E3.0.2.13"),sQuery(id+"F0.wireOp",EDGE,"E3.0.2.14"),sQuery(id+"F0.wireOp",EDGE,"E3.0.2.15"),subQ26,sQuery(id+"F0.wireOp",EDGE,"E3.0.3.0"),sQuery(id+"F0.wireOp",EDGE,"E3.0.3.1"),sQuery(id+"F0.wireOp",EDGE,"E3.0.3.2"),sQuery(id+"F0.wireOp",EDGE,"E3.0.3.3"),sQuery(id+"F0.wireOp",EDGE,"E3.0.3.4"),sQuery(id+"F0.wireOp",EDGE,"E3.0.3.5"),sQuery(id+"F0.wireOp",EDGE,"E3.0.3.6"),sQuery(id+"F0.wireOp",EDGE,"E3.0.3.7"),sQuery(id+"F0.wireOp",EDGE,"E3.0.3.8"),sQuery(id+"F0.wireOp",EDGE,"E3.0.3.9"),sQuery(id+"F0.wireOp",EDGE,"E3.0.3.10"),sQuery(id+"F0.wireOp",EDGE,"E3.0.3.11"),sQuery(id+"F0.wireOp",EDGE,"E3.0.3.12"),sQuery(id+"F0.wireOp",EDGE,"E3.0.3.13"),sQuery(id+"F0.wireOp",EDGE,"E3.0.3.14"),sQuery(id+"F0.wireOp",EDGE,"E3.0.3.15"),subQ28,sQuery(id+"F0.wireOp",EDGE,"E3.0.4.0"),sQuery(id+"F0.wireOp",EDGE,"E3.0.4.1"),sQuery(id+"F0.wireOp",EDGE,"E3.0.4.2"),sQuery(id+"F0.wireOp",EDGE,"E3.0.4.3"),sQuery(id+"F0.wireOp",EDGE,"E3.0.4.4"),sQuery(id+"F0.wireOp",EDGE,"E3.0.4.5"),sQuery(id+"F0.wireOp",EDGE,"E3.0.4.6"),sQuery(id+"F0.wireOp",EDGE,"E3.0.4.7"),sQuery(id+"F0.wireOp",EDGE,"E3.0.4.8"),sQuery(id+"F0.wireOp",EDGE,"E3.0.4.9"),sQuery(id+"F0.wireOp",EDGE,"E3.0.4.10"),sQuery(id+"F0.wireOp",EDGE,"E3.0.4.11"),sQuery(id+"F0.wireOp",EDGE,"E3.0.4.12"),sQuery(id+"F0.wireOp",EDGE,"E3.0.4.13"),sQuery(id+"F0.wireOp",EDGE,"E3.0.4.14"),sQuery(id+"F0.wireOp",EDGE,"E3.0.4.15"),subQ29,sQuery(id+"F0.wireOp",EDGE,"E3.0.5.0"),sQuery(id+"F0.wireOp",EDGE,"E3.0.5.1"),sQuery(id+"F0.wireOp",EDGE,"E3.0.5.2"),sQuery(id+"F0.wireOp",EDGE,"E3.0.5.3"),sQuery(id+"F0.wireOp",EDGE,"E3.0.5.4"),sQuery(id+"F0.wireOp",EDGE,"E3.0.5.5"),sQuery(id+"F0.wireOp",EDGE,"E3.0.5.6"),sQuery(id+"F0.wireOp",EDGE,"E3.0.5.7"),sQuery(id+"F0.wireOp",EDGE,"E3.0.5.8"),sQuery(id+"F0.wireOp",EDGE,"E3.0.5.9"),sQuery(id+"F0.wireOp",EDGE,"E3.0.5.10"),sQuery(id+"F0.wireOp",EDGE,"E3.0.5.11"),sQuery(id+"F0.wireOp",EDGE,"E3.0.5.12"),sQuery(id+"F0.wireOp",EDGE,"E3.0.5.13"),sQuery(id+"F0.wireOp",EDGE,"E3.0.5.14"),sQuery(id+"F0.wireOp",EDGE,"E3.0.5.15"),subQ30,sQuery(id+"F0.wireOp",EDGE,"E3.0.6.0"),sQuery(id+"F0.wireOp",EDGE,"E3.0.6.1"),sQuery(id+"F0.wireOp",EDGE,"E3.0.6.2"),sQuery(id+"F0.wireOp",EDGE,"E3.0.6.3"),sQuery(id+"F0.wireOp",EDGE,"E3.0.6.4"),sQuery(id+"F0.wireOp",EDGE,"E3.0.6.5"),sQuery(id+"F0.wireOp",EDGE,"E3.0.6.6"),sQuery(id+"F0.wireOp",EDGE,"E3.0.6.7"),sQuery(id+"F0.wireOp",EDGE,"E3.0.6.8"),sQuery(id+"F0.wireOp",EDGE,"E3.0.6.9"),sQuery(id+"F0.wireOp",EDGE,"E3.0.6.10"),sQuery(id+"F0.wireOp",EDGE,"E3.0.6.11"),sQuery(id+"F0.wireOp",EDGE,"E3.0.6.12"),sQuery(id+"F0.wireOp",EDGE,"E3.0.6.13"),sQuery(id+"F0.wireOp",EDGE,"E3.0.6.14"),sQuery(id+"F0.wireOp",EDGE,"E3.0.6.15"),subQ7,sQuery(id+"F0.wireOp",EDGE,"E3.0.7.0"),sQuery(id+"F0.wireOp",EDGE,"E3.0.7.1"),sQuery(id+"F0.wireOp",EDGE,"E3.0.7.2"),sQuery(id+"F0.wireOp",EDGE,"E3.0.7.3"),sQuery(id+"F0.wireOp",EDGE,"E3.0.7.4"),sQuery(id+"F0.wireOp",EDGE,"E3.0.7.5"),sQuery(id+"F0.wireOp",EDGE,"E3.0.7.6"),sQuery(id+"F0.wireOp",EDGE,"E3.0.7.7"),sQuery(id+"F0.wireOp",EDGE,"E3.0.7.8"),sQuery(id+"F0.wireOp",EDGE,"E3.0.7.9"),sQuery(id+"F0.wireOp",EDGE,"E3.0.7.10"),sQuery(id+"F0.wireOp",EDGE,"E3.0.7.11"),sQuery(id+"F0.wireOp",EDGE,"E3.0.7.12"),sQuery(id+"F0.wireOp",EDGE,"E3.0.7.13"),sQuery(id+"F0.wireOp",EDGE,"E3.0.7.14"),sQuery(id+"F0.wireOp",EDGE,"E3.0.7.15"),subQ31,sQuery(id+"F0.wireOp",EDGE,"E3.0.8.0"),sQuery(id+"F0.wireOp",EDGE,"E3.0.8.1"),sQuery(id+"F0.wireOp",EDGE,"E3.0.8.2"),sQuery(id+"F0.wireOp",EDGE,"E3.0.8.3"),sQuery(id+"F0.wireOp",EDGE,"E3.0.8.4"),sQuery(id+"F0.wireOp",EDGE,"E3.0.8.5"),sQuery(id+"F0.wireOp",EDGE,"E3.0.8.6"),sQuery(id+"F0.wireOp",EDGE,"E3.0.8.7"),sQuery(id+"F0.wireOp",EDGE,"E3.0.8.8"),sQuery(id+"F0.wireOp",EDGE,"E3.0.8.9"),sQuery(id+"F0.wireOp",EDGE,"E3.0.8.10"),sQuery(id+"F0.wireOp",EDGE,"E3.0.8.11"),sQuery(id+"F0.wireOp",EDGE,"E3.0.8.12"),sQuery(id+"F0.wireOp",EDGE,"E3.0.8.13"),sQuery(id+"F0.wireOp",EDGE,"E3.0.8.14"),sQuery(id+"F0.wireOp",EDGE,"E3.0.8.15"),subQ14,sQuery(id+"F0.wireOp",EDGE,"E3.0.9.0"),sQuery(id+"F0.wireOp",EDGE,"E3.0.9.1"),sQuery(id+"F0.wireOp",EDGE,"E3.0.9.2"),sQuery(id+"F0.wireOp",EDGE,"E3.0.9.3"),sQuery(id+"F0.wireOp",EDGE,"E3.0.9.4"),sQuery(id+"F0.wireOp",EDGE,"E3.0.9.5"),sQuery(id+"F0.wireOp",EDGE,"E3.0.9.6"),sQuery(id+"F0.wireOp",EDGE,"E3.0.9.7"),sQuery(id+"F0.wireOp",EDGE,"E3.0.9.8"),sQuery(id+"F0.wireOp",EDGE,"E3.0.9.9"),sQuery(id+"F0.wireOp",EDGE,"E3.0.9.10"),sQuery(id+"F0.wireOp",EDGE,"E3.0.9.11"),sQuery(id+"F0.wireOp",EDGE,"E3.0.9.12"),sQuery(id+"F0.wireOp",EDGE,"E3.0.9.13"),sQuery(id+"F0.wireOp",EDGE,"E3.0.9.14"),sQuery(id+"F0.wireOp",EDGE,"E3.0.9.15"),subQ8,sQuery(id+"F0.wireOp",EDGE,"E3.0.10.0"),sQuery(id+"F0.wireOp",EDGE,"E3.0.10.1"),sQuery(id+"F0.wireOp",EDGE,"E3.0.10.2"),sQuery(id+"F0.wireOp",EDGE,"E3.0.10.3"),sQuery(id+"F0.wireOp",EDGE,"E3.0.10.4"),sQuery(id+"F0.wireOp",EDGE,"E3.0.10.5"),sQuery(id+"F0.wireOp",EDGE,"E3.0.10.6"),sQuery(id+"F0.wireOp",EDGE,"E3.0.10.7"),sQuery(id+"F0.wireOp",EDGE,"E3.0.10.8"),sQuery(id+"F0.wireOp",EDGE,"E3.0.10.9"),sQuery(id+"F0.wireOp",EDGE,"E3.0.10.10"),sQuery(id+"F0.wireOp",EDGE,"E3.0.10.11"),sQuery(id+"F0.wireOp",EDGE,"E3.0.10.12"),sQuery(id+"F0.wireOp",EDGE,"E3.0.10.13"),sQuery(id+"F0.wireOp",EDGE,"E3.0.10.14"),sQuery(id+"F0.wireOp",EDGE,"E3.0.10.15"),subQ21,sQuery(id+"F0.wireOp",EDGE,"E3.0.11.0"),sQuery(id+"F0.wireOp",EDGE,"E3.0.11.1"),sQuery(id+"F0.wireOp",EDGE,"E3.0.11.2"),sQuery(id+"F0.wireOp",EDGE,"E3.0.11.3"),sQuery(id+"F0.wireOp",EDGE,"E3.0.11.4"),sQuery(id+"F0.wireOp",EDGE,"E3.0.11.5"),sQuery(id+"F0.wireOp",EDGE,"E3.0.11.6"),sQuery(id+"F0.wireOp",EDGE,"E3.0.11.7"),sQuery(id+"F0.wireOp",EDGE,"E3.0.11.8"),sQuery(id+"F0.wireOp",EDGE,"E3.0.11.9"),sQuery(id+"F0.wireOp",EDGE,"E3.0.11.10"),sQuery(id+"F0.wireOp",EDGE,"E3.0.11.11"),sQuery(id+"F0.wireOp",EDGE,"E3.0.11.12"),sQuery(id+"F0.wireOp",EDGE,"E3.0.11.13"),sQuery(id+"F0.wireOp",EDGE,"E3.0.11.14"),sQuery(id+"F0.wireOp",EDGE,"E3.0.11.15"),subQ32,sQuery(id+"F0.wireOp",EDGE,"E3.0.12.0"),sQuery(id+"F0.wireOp",EDGE,"E3.0.12.1"),sQuery(id+"F0.wireOp",EDGE,"E3.0.12.2"),sQuery(id+"F0.wireOp",EDGE,"E3.0.12.3"),sQuery(id+"F0.wireOp",EDGE,"E3.0.12.4"),sQuery(id+"F0.wireOp",EDGE,"E3.0.12.5"),sQuery(id+"F0.wireOp",EDGE,"E3.0.12.6"),sQuery(id+"F0.wireOp",EDGE,"E3.0.12.7"),sQuery(id+"F0.wireOp",EDGE,"E3.0.12.8"),sQuery(id+"F0.wireOp",EDGE,"E3.0.12.9"),sQuery(id+"F0.wireOp",EDGE,"E3.0.12.10"),sQuery(id+"F0.wireOp",EDGE,"E3.0.12.11"),sQuery(id+"F0.wireOp",EDGE,"E3.0.12.12"),sQuery(id+"F0.wireOp",EDGE,"E3.0.12.13"),sQuery(id+"F0.wireOp",EDGE,"E3.0.12.14"),sQuery(id+"F0.wireOp",EDGE,"E3.0.12.15"),subQ33,sQuery(id+"F0.wireOp",EDGE,"E3.0.13.0"),sQuery(id+"F0.wireOp",EDGE,"E3.0.13.1"),sQuery(id+"F0.wireOp",EDGE,"E3.0.13.2"),sQuery(id+"F0.wireOp",EDGE,"E3.0.13.3"),sQuery(id+"F0.wireOp",EDGE,"E3.0.13.4"),sQuery(id+"F0.wireOp",EDGE,"E3.0.13.5"),sQuery(id+"F0.wireOp",EDGE,"E3.0.13.6"),sQuery(id+"F0.wireOp",EDGE,"E3.0.13.7"),sQuery(id+"F0.wireOp",EDGE,"E3.0.13.8"),sQuery(id+"F0.wireOp",EDGE,"E3.0.13.9"),sQuery(id+"F0.wireOp",EDGE,"E3.0.13.10"),sQuery(id+"F0.wireOp",EDGE,"E3.0.13.11"),sQuery(id+"F0.wireOp",EDGE,"E3.0.13.12"),sQuery(id+"F0.wireOp",EDGE,"E3.0.13.13"),sQuery(id+"F0.wireOp",EDGE,"E3.0.13.14"),sQuery(id+"F0.wireOp",EDGE,"E3.0.13.15"),subQ34,sQuery(id+"F0.wireOp",EDGE,"E3.0.14.0"),sQuery(id+"F0.wireOp",EDGE,"E3.0.14.1"),sQuery(id+"F0.wireOp",EDGE,"E3.0.14.2"),sQuery(id+"F0.wireOp",EDGE,"E3.0.14.3"),sQuery(id+"F0.wireOp",EDGE,"E3.0.14.4"),sQuery(id+"F0.wireOp",EDGE,"E3.0.14.5"),sQuery(id+"F0.wireOp",EDGE,"E3.0.14.6"),sQuery(id+"F0.wireOp",EDGE,"E3.0.14.7"),sQuery(id+"F0.wireOp",EDGE,"E3.0.14.8"),sQuery(id+"F0.wireOp",EDGE,"E3.0.14.9"),sQuery(id+"F0.wireOp",EDGE,"E3.0.14.10"),sQuery(id+"F0.wireOp",EDGE,"E3.0.14.11"),sQuery(id+"F0.wireOp",EDGE,"E3.0.14.12"),sQuery(id+"F0.wireOp",EDGE,"E3.0.14.13"),sQuery(id+"F0.wireOp",EDGE,"E3.0.14.14"),sQuery(id+"F0.wireOp",EDGE,"E3.0.14.15"),subQ11,sQuery(id+"F0.wireOp",EDGE,"E3.0.15.0"),sQuery(id+"F0.wireOp",EDGE,"E3.0.15.1"),sQuery(id+"F0.wireOp",EDGE,"E3.0.15.2"),sQuery(id+"F0.wireOp",EDGE,"E3.0.15.3"),sQuery(id+"F0.wireOp",EDGE,"E3.0.15.4"),sQuery(id+"F0.wireOp",EDGE,"E3.0.15.5"),sQuery(id+"F0.wireOp",EDGE,"E3.0.15.6"),sQuery(id+"F0.wireOp",EDGE,"E3.0.15.7"),sQuery(id+"F0.wireOp",EDGE,"E3.0.15.8"),sQuery(id+"F0.wireOp",EDGE,"E3.0.15.9"),sQuery(id+"F0.wireOp",EDGE,"E3.0.15.10"),sQuery(id+"F0.wireOp",EDGE,"E3.0.15.11"),sQuery(id+"F0.wireOp",EDGE,"E3.0.15.12"),sQuery(id+"F0.wireOp",EDGE,"E3.0.15.13"),sQuery(id+"F0.wireOp",EDGE,"E3.0.15.14"),sQuery(id+"F0.wireOp",EDGE,"E3.0.15.15"),subQ35,sQuery(id+"F0.wireOp",EDGE,"E3.0.16.0"),sQuery(id+"F0.wireOp",EDGE,"E3.0.16.1"),sQuery(id+"F0.wireOp",EDGE,"E3.0.16.2"),sQuery(id+"F0.wireOp",EDGE,"E3.0.16.3"),sQuery(id+"F0.wireOp",EDGE,"E3.0.16.4"),sQuery(id+"F0.wireOp",EDGE,"E3.0.16.5"),sQuery(id+"F0.wireOp",EDGE,"E3.0.16.6"),sQuery(id+"F0.wireOp",EDGE,"E3.0.16.7"),sQuery(id+"F0.wireOp",EDGE,"E3.0.16.8"),sQuery(id+"F0.wireOp",EDGE,"E3.0.16.9"),sQuery(id+"F0.wireOp",EDGE,"E3.0.16.10"),sQuery(id+"F0.wireOp",EDGE,"E3.0.16.11"),sQuery(id+"F0.wireOp",EDGE,"E3.0.16.12"),sQuery(id+"F0.wireOp",EDGE,"E3.0.16.13"),sQuery(id+"F0.wireOp",EDGE,"E3.0.16.14"),sQuery(id+"F0.wireOp",EDGE,"E3.0.16.15"),subQ36])],"isStart":false})});}
            var sketch = newSketch(context, id + "F4", { "sketchPlane" : qUnion([Q0])});
            skLineSegment(sketch, "E10.bottom", {"start": v(-20.75, -83) * mm, "end": v(-19.25, -83) * mm});
            skLineSegment(sketch, "E10.top", {"start": v(-20.75, -96.59) * mm, "end": v(-19.25, -96.59) * mm});
            skLineSegment(sketch, "E10.left", {"start": v(-20.75, -83) * mm, "end": v(-20.75, -96.59) * mm});
            skLineSegment(sketch, "E10.right", {"start": v(-19.25, -83) * mm, "end": v(-19.25, -96.59) * mm});
            skLineSegment(sketch, "E11.bottom", {"start": v(39.25, -83) * mm, "end": v(40.75, -83) * mm});
            skLineSegment(sketch, "E11.top", {"start": v(39.25, -99.25) * mm, "end": v(40.75, -99.25) * mm});
            skLineSegment(sketch, "E11.left", {"start": v(39.25, -83) * mm, "end": v(39.25, -99.25) * mm});
            skLineSegment(sketch, "E11.right", {"start": v(40.75, -83) * mm, "end": v(40.75, -99.25) * mm});
            skLineSegment(sketch, "E12.bottom", {"start": v(-80, -22.25) * mm, "end": v(-98.85, -22.25) * mm});
            skLineSegment(sketch, "E12.top", {"start": v(-80, -23.75) * mm, "end": v(-98.85, -23.75) * mm});
            skLineSegment(sketch, "E12.left", {"start": v(-98.85, -22.25) * mm, "end": v(-98.85, -23.75) * mm});
            skLineSegment(sketch, "E12.right", {"start": v(-80, -22.25) * mm, "end": v(-80, -23.75) * mm});
            skPoint(sketch, "E13.oppositeSnap0", {"position": v(-84.48, 36.25) * mm});
            skLineSegment(sketch, "E13.bottom", {"start": v(-80, 37.75) * mm, "end": v(-100.24, 37.75) * mm});
            skLineSegment(sketch, "E13.top", {"start": v(-80, 36.25) * mm, "end": v(-100.24, 36.25) * mm});
            skLineSegment(sketch, "E13.left", {"start": v(-80, 37.75) * mm, "end": v(-80, 36.25) * mm});
            skLineSegment(sketch, "E13.right", {"start": v(-100.24, 37.75) * mm, "end": v(-100.24, 36.25) * mm});
            skSolve(sketch);
        }
        {
            var Q0;
            {var subQ0=sQuery(id+"F0.wireOp",EDGE,"E3.0.1.16");var subQ1=sQuery(id+"F0.wireOp",EDGE,"6f7ae5fc-1566-4385-bfb5-e6e9eca27b98.0.0.16");var subQ2=sQuery(id+"F0.wireOp",EDGE,"E2.0.8.0");var subQ3=sQuery(id+"F0.wireOp",EDGE,"E2.0.9.0");var subQ4=sQuery(id+"F0.wireOp",EDGE,"E2.0.15.0");var subQ5=sQuery(id+"F0.wireOp",EDGE,"E2.0.14.0");var subQ6=sQuery(id+"F0.wireOp",EDGE,"E2.0.6.0");var subQ7=sQuery(id+"F0.wireOp",EDGE,"E3.0.6.16");var subQ8=sQuery(id+"F0.wireOp",EDGE,"E3.0.9.16");var subQ9=sQuery(id+"F0.wireOp",EDGE,"E2.0.13.0");var subQ10=sQuery(id+"F0.wireOp",EDGE,"E2.0.11.0");var subQ11=sQuery(id+"F0.wireOp",EDGE,"E3.0.14.16");var subQ12=sQuery(id+"F0.wireOp",EDGE,"E2.0.7.0");var subQ13=sQuery(id+"F0.wireOp",EDGE,"E0.right");var subQ14=sQuery(id+"F0.wireOp",EDGE,"E3.0.8.16");var subQ15=sQuery(id+"F0.wireOp",EDGE,"E0.left");var subQ16=sQuery(id+"F0.wireOp",EDGE,"E0.top");var subQ17=sQuery(id+"F0.wireOp",EDGE,"E2.0.4.0");var subQ18=sQuery(id+"F0.wireOp",EDGE,"E2.0.12.0");var subQ19=sQuery(id+"F0.wireOp",EDGE,"E0.bottom");var subQ20=sQuery(id+"F0.wireOp",EDGE,"E1");var subQ21=sQuery(id+"F0.wireOp",EDGE,"E3.0.10.16");var subQ22=sQuery(id+"F0.wireOp",EDGE,"E2.0.1.0");var subQ23=sQuery(id+"F0.wireOp",EDGE,"E2.0.2.0");var subQ24=sQuery(id+"F0.wireOp",EDGE,"E2.0.10.0");var subQ25=sQuery(id+"F0.wireOp",EDGE,"E2.0.3.0");var subQ26=sQuery(id+"F0.wireOp",EDGE,"E3.0.2.16");var subQ27=sQuery(id+"F0.wireOp",EDGE,"E2.0.5.0");var subQ28=sQuery(id+"F0.wireOp",EDGE,"E3.0.3.16");var subQ29=sQuery(id+"F0.wireOp",EDGE,"E3.0.4.16");var subQ30=sQuery(id+"F0.wireOp",EDGE,"E3.0.5.16");var subQ31=sQuery(id+"F0.wireOp",EDGE,"E3.0.7.16");var subQ32=sQuery(id+"F0.wireOp",EDGE,"E3.0.11.16");var subQ33=sQuery(id+"F0.wireOp",EDGE,"E3.0.12.16");var subQ34=sQuery(id+"F0.wireOp",EDGE,"E3.0.13.16");var subQ35=sQuery(id+"F0.wireOp",EDGE,"E3.0.15.16");var subQ36=sQuery(id+"F0.wireOp",EDGE,"E3.0.16.16");Q0=makeQuery(id+"FJqtpdUANZnq3Um_1.boolean.opBoolean","SPLIT",FACE,{"disambiguationData":[TD([makeQuery(id+"F1.opExtrude","SWEPT_FACE",FACE,{"disambiguationData":[OSD([subQ19])]})])],"derivedFrom":makeQuery(id+"F1.opExtrude","CAP_FACE",FACE,{"disambiguationData":[OSD([subQ19,subQ16,subQ15,subQ13,subQ20,subQ22,subQ23,subQ25,subQ17,subQ27,subQ6,subQ12,subQ2,subQ3,subQ24,subQ10,subQ18,subQ9,subQ5,subQ4,subQ1,sQuery(id+"F0.wireOp",EDGE,"E3.0.1.0"),sQuery(id+"F0.wireOp",EDGE,"E3.0.1.1"),sQuery(id+"F0.wireOp",EDGE,"E3.0.1.2"),sQuery(id+"F0.wireOp",EDGE,"E3.0.1.3"),sQuery(id+"F0.wireOp",EDGE,"E3.0.1.4"),sQuery(id+"F0.wireOp",EDGE,"E3.0.1.5"),sQuery(id+"F0.wireOp",EDGE,"E3.0.1.6"),sQuery(id+"F0.wireOp",EDGE,"E3.0.1.7"),sQuery(id+"F0.wireOp",EDGE,"E3.0.1.8"),sQuery(id+"F0.wireOp",EDGE,"E3.0.1.9"),sQuery(id+"F0.wireOp",EDGE,"E3.0.1.10"),sQuery(id+"F0.wireOp",EDGE,"E3.0.1.11"),sQuery(id+"F0.wireOp",EDGE,"E3.0.1.12"),sQuery(id+"F0.wireOp",EDGE,"E3.0.1.13"),sQuery(id+"F0.wireOp",EDGE,"E3.0.1.14"),sQuery(id+"F0.wireOp",EDGE,"E3.0.1.15"),subQ0,sQuery(id+"F0.wireOp",EDGE,"E3.0.2.0"),sQuery(id+"F0.wireOp",EDGE,"E3.0.2.1"),sQuery(id+"F0.wireOp",EDGE,"E3.0.2.2"),sQuery(id+"F0.wireOp",EDGE,"E3.0.2.3"),sQuery(id+"F0.wireOp",EDGE,"E3.0.2.4"),sQuery(id+"F0.wireOp",EDGE,"E3.0.2.5"),sQuery(id+"F0.wireOp",EDGE,"E3.0.2.6"),sQuery(id+"F0.wireOp",EDGE,"E3.0.2.7"),sQuery(id+"F0.wireOp",EDGE,"E3.0.2.8"),sQuery(id+"F0.wireOp",EDGE,"E3.0.2.9"),sQuery(id+"F0.wireOp",EDGE,"E3.0.2.10"),sQuery(id+"F0.wireOp",EDGE,"E3.0.2.11"),sQuery(id+"F0.wireOp",EDGE,"E3.0.2.12"),sQuery(id+"F0.wireOp",EDGE,"E3.0.2.13"),sQuery(id+"F0.wireOp",EDGE,"E3.0.2.14"),sQuery(id+"F0.wireOp",EDGE,"E3.0.2.15"),subQ26,sQuery(id+"F0.wireOp",EDGE,"E3.0.3.0"),sQuery(id+"F0.wireOp",EDGE,"E3.0.3.1"),sQuery(id+"F0.wireOp",EDGE,"E3.0.3.2"),sQuery(id+"F0.wireOp",EDGE,"E3.0.3.3"),sQuery(id+"F0.wireOp",EDGE,"E3.0.3.4"),sQuery(id+"F0.wireOp",EDGE,"E3.0.3.5"),sQuery(id+"F0.wireOp",EDGE,"E3.0.3.6"),sQuery(id+"F0.wireOp",EDGE,"E3.0.3.7"),sQuery(id+"F0.wireOp",EDGE,"E3.0.3.8"),sQuery(id+"F0.wireOp",EDGE,"E3.0.3.9"),sQuery(id+"F0.wireOp",EDGE,"E3.0.3.10"),sQuery(id+"F0.wireOp",EDGE,"E3.0.3.11"),sQuery(id+"F0.wireOp",EDGE,"E3.0.3.12"),sQuery(id+"F0.wireOp",EDGE,"E3.0.3.13"),sQuery(id+"F0.wireOp",EDGE,"E3.0.3.14"),sQuery(id+"F0.wireOp",EDGE,"E3.0.3.15"),subQ28,sQuery(id+"F0.wireOp",EDGE,"E3.0.4.0"),sQuery(id+"F0.wireOp",EDGE,"E3.0.4.1"),sQuery(id+"F0.wireOp",EDGE,"E3.0.4.2"),sQuery(id+"F0.wireOp",EDGE,"E3.0.4.3"),sQuery(id+"F0.wireOp",EDGE,"E3.0.4.4"),sQuery(id+"F0.wireOp",EDGE,"E3.0.4.5"),sQuery(id+"F0.wireOp",EDGE,"E3.0.4.6"),sQuery(id+"F0.wireOp",EDGE,"E3.0.4.7"),sQuery(id+"F0.wireOp",EDGE,"E3.0.4.8"),sQuery(id+"F0.wireOp",EDGE,"E3.0.4.9"),sQuery(id+"F0.wireOp",EDGE,"E3.0.4.10"),sQuery(id+"F0.wireOp",EDGE,"E3.0.4.11"),sQuery(id+"F0.wireOp",EDGE,"E3.0.4.12"),sQuery(id+"F0.wireOp",EDGE,"E3.0.4.13"),sQuery(id+"F0.wireOp",EDGE,"E3.0.4.14"),sQuery(id+"F0.wireOp",EDGE,"E3.0.4.15"),subQ29,sQuery(id+"F0.wireOp",EDGE,"E3.0.5.0"),sQuery(id+"F0.wireOp",EDGE,"E3.0.5.1"),sQuery(id+"F0.wireOp",EDGE,"E3.0.5.2"),sQuery(id+"F0.wireOp",EDGE,"E3.0.5.3"),sQuery(id+"F0.wireOp",EDGE,"E3.0.5.4"),sQuery(id+"F0.wireOp",EDGE,"E3.0.5.5"),sQuery(id+"F0.wireOp",EDGE,"E3.0.5.6"),sQuery(id+"F0.wireOp",EDGE,"E3.0.5.7"),sQuery(id+"F0.wireOp",EDGE,"E3.0.5.8"),sQuery(id+"F0.wireOp",EDGE,"E3.0.5.9"),sQuery(id+"F0.wireOp",EDGE,"E3.0.5.10"),sQuery(id+"F0.wireOp",EDGE,"E3.0.5.11"),sQuery(id+"F0.wireOp",EDGE,"E3.0.5.12"),sQuery(id+"F0.wireOp",EDGE,"E3.0.5.13"),sQuery(id+"F0.wireOp",EDGE,"E3.0.5.14"),sQuery(id+"F0.wireOp",EDGE,"E3.0.5.15"),subQ30,sQuery(id+"F0.wireOp",EDGE,"E3.0.6.0"),sQuery(id+"F0.wireOp",EDGE,"E3.0.6.1"),sQuery(id+"F0.wireOp",EDGE,"E3.0.6.2"),sQuery(id+"F0.wireOp",EDGE,"E3.0.6.3"),sQuery(id+"F0.wireOp",EDGE,"E3.0.6.4"),sQuery(id+"F0.wireOp",EDGE,"E3.0.6.5"),sQuery(id+"F0.wireOp",EDGE,"E3.0.6.6"),sQuery(id+"F0.wireOp",EDGE,"E3.0.6.7"),sQuery(id+"F0.wireOp",EDGE,"E3.0.6.8"),sQuery(id+"F0.wireOp",EDGE,"E3.0.6.9"),sQuery(id+"F0.wireOp",EDGE,"E3.0.6.10"),sQuery(id+"F0.wireOp",EDGE,"E3.0.6.11"),sQuery(id+"F0.wireOp",EDGE,"E3.0.6.12"),sQuery(id+"F0.wireOp",EDGE,"E3.0.6.13"),sQuery(id+"F0.wireOp",EDGE,"E3.0.6.14"),sQuery(id+"F0.wireOp",EDGE,"E3.0.6.15"),subQ7,sQuery(id+"F0.wireOp",EDGE,"E3.0.7.0"),sQuery(id+"F0.wireOp",EDGE,"E3.0.7.1"),sQuery(id+"F0.wireOp",EDGE,"E3.0.7.2"),sQuery(id+"F0.wireOp",EDGE,"E3.0.7.3"),sQuery(id+"F0.wireOp",EDGE,"E3.0.7.4"),sQuery(id+"F0.wireOp",EDGE,"E3.0.7.5"),sQuery(id+"F0.wireOp",EDGE,"E3.0.7.6"),sQuery(id+"F0.wireOp",EDGE,"E3.0.7.7"),sQuery(id+"F0.wireOp",EDGE,"E3.0.7.8"),sQuery(id+"F0.wireOp",EDGE,"E3.0.7.9"),sQuery(id+"F0.wireOp",EDGE,"E3.0.7.10"),sQuery(id+"F0.wireOp",EDGE,"E3.0.7.11"),sQuery(id+"F0.wireOp",EDGE,"E3.0.7.12"),sQuery(id+"F0.wireOp",EDGE,"E3.0.7.13"),sQuery(id+"F0.wireOp",EDGE,"E3.0.7.14"),sQuery(id+"F0.wireOp",EDGE,"E3.0.7.15"),subQ31,sQuery(id+"F0.wireOp",EDGE,"E3.0.8.0"),sQuery(id+"F0.wireOp",EDGE,"E3.0.8.1"),sQuery(id+"F0.wireOp",EDGE,"E3.0.8.2"),sQuery(id+"F0.wireOp",EDGE,"E3.0.8.3"),sQuery(id+"F0.wireOp",EDGE,"E3.0.8.4"),sQuery(id+"F0.wireOp",EDGE,"E3.0.8.5"),sQuery(id+"F0.wireOp",EDGE,"E3.0.8.6"),sQuery(id+"F0.wireOp",EDGE,"E3.0.8.7"),sQuery(id+"F0.wireOp",EDGE,"E3.0.8.8"),sQuery(id+"F0.wireOp",EDGE,"E3.0.8.9"),sQuery(id+"F0.wireOp",EDGE,"E3.0.8.10"),sQuery(id+"F0.wireOp",EDGE,"E3.0.8.11"),sQuery(id+"F0.wireOp",EDGE,"E3.0.8.12"),sQuery(id+"F0.wireOp",EDGE,"E3.0.8.13"),sQuery(id+"F0.wireOp",EDGE,"E3.0.8.14"),sQuery(id+"F0.wireOp",EDGE,"E3.0.8.15"),subQ14,sQuery(id+"F0.wireOp",EDGE,"E3.0.9.0"),sQuery(id+"F0.wireOp",EDGE,"E3.0.9.1"),sQuery(id+"F0.wireOp",EDGE,"E3.0.9.2"),sQuery(id+"F0.wireOp",EDGE,"E3.0.9.3"),sQuery(id+"F0.wireOp",EDGE,"E3.0.9.4"),sQuery(id+"F0.wireOp",EDGE,"E3.0.9.5"),sQuery(id+"F0.wireOp",EDGE,"E3.0.9.6"),sQuery(id+"F0.wireOp",EDGE,"E3.0.9.7"),sQuery(id+"F0.wireOp",EDGE,"E3.0.9.8"),sQuery(id+"F0.wireOp",EDGE,"E3.0.9.9"),sQuery(id+"F0.wireOp",EDGE,"E3.0.9.10"),sQuery(id+"F0.wireOp",EDGE,"E3.0.9.11"),sQuery(id+"F0.wireOp",EDGE,"E3.0.9.12"),sQuery(id+"F0.wireOp",EDGE,"E3.0.9.13"),sQuery(id+"F0.wireOp",EDGE,"E3.0.9.14"),sQuery(id+"F0.wireOp",EDGE,"E3.0.9.15"),subQ8,sQuery(id+"F0.wireOp",EDGE,"E3.0.10.0"),sQuery(id+"F0.wireOp",EDGE,"E3.0.10.1"),sQuery(id+"F0.wireOp",EDGE,"E3.0.10.2"),sQuery(id+"F0.wireOp",EDGE,"E3.0.10.3"),sQuery(id+"F0.wireOp",EDGE,"E3.0.10.4"),sQuery(id+"F0.wireOp",EDGE,"E3.0.10.5"),sQuery(id+"F0.wireOp",EDGE,"E3.0.10.6"),sQuery(id+"F0.wireOp",EDGE,"E3.0.10.7"),sQuery(id+"F0.wireOp",EDGE,"E3.0.10.8"),sQuery(id+"F0.wireOp",EDGE,"E3.0.10.9"),sQuery(id+"F0.wireOp",EDGE,"E3.0.10.10"),sQuery(id+"F0.wireOp",EDGE,"E3.0.10.11"),sQuery(id+"F0.wireOp",EDGE,"E3.0.10.12"),sQuery(id+"F0.wireOp",EDGE,"E3.0.10.13"),sQuery(id+"F0.wireOp",EDGE,"E3.0.10.14"),sQuery(id+"F0.wireOp",EDGE,"E3.0.10.15"),subQ21,sQuery(id+"F0.wireOp",EDGE,"E3.0.11.0"),sQuery(id+"F0.wireOp",EDGE,"E3.0.11.1"),sQuery(id+"F0.wireOp",EDGE,"E3.0.11.2"),sQuery(id+"F0.wireOp",EDGE,"E3.0.11.3"),sQuery(id+"F0.wireOp",EDGE,"E3.0.11.4"),sQuery(id+"F0.wireOp",EDGE,"E3.0.11.5"),sQuery(id+"F0.wireOp",EDGE,"E3.0.11.6"),sQuery(id+"F0.wireOp",EDGE,"E3.0.11.7"),sQuery(id+"F0.wireOp",EDGE,"E3.0.11.8"),sQuery(id+"F0.wireOp",EDGE,"E3.0.11.9"),sQuery(id+"F0.wireOp",EDGE,"E3.0.11.10"),sQuery(id+"F0.wireOp",EDGE,"E3.0.11.11"),sQuery(id+"F0.wireOp",EDGE,"E3.0.11.12"),sQuery(id+"F0.wireOp",EDGE,"E3.0.11.13"),sQuery(id+"F0.wireOp",EDGE,"E3.0.11.14"),sQuery(id+"F0.wireOp",EDGE,"E3.0.11.15"),subQ32,sQuery(id+"F0.wireOp",EDGE,"E3.0.12.0"),sQuery(id+"F0.wireOp",EDGE,"E3.0.12.1"),sQuery(id+"F0.wireOp",EDGE,"E3.0.12.2"),sQuery(id+"F0.wireOp",EDGE,"E3.0.12.3"),sQuery(id+"F0.wireOp",EDGE,"E3.0.12.4"),sQuery(id+"F0.wireOp",EDGE,"E3.0.12.5"),sQuery(id+"F0.wireOp",EDGE,"E3.0.12.6"),sQuery(id+"F0.wireOp",EDGE,"E3.0.12.7"),sQuery(id+"F0.wireOp",EDGE,"E3.0.12.8"),sQuery(id+"F0.wireOp",EDGE,"E3.0.12.9"),sQuery(id+"F0.wireOp",EDGE,"E3.0.12.10"),sQuery(id+"F0.wireOp",EDGE,"E3.0.12.11"),sQuery(id+"F0.wireOp",EDGE,"E3.0.12.12"),sQuery(id+"F0.wireOp",EDGE,"E3.0.12.13"),sQuery(id+"F0.wireOp",EDGE,"E3.0.12.14"),sQuery(id+"F0.wireOp",EDGE,"E3.0.12.15"),subQ33,sQuery(id+"F0.wireOp",EDGE,"E3.0.13.0"),sQuery(id+"F0.wireOp",EDGE,"E3.0.13.1"),sQuery(id+"F0.wireOp",EDGE,"E3.0.13.2"),sQuery(id+"F0.wireOp",EDGE,"E3.0.13.3"),sQuery(id+"F0.wireOp",EDGE,"E3.0.13.4"),sQuery(id+"F0.wireOp",EDGE,"E3.0.13.5"),sQuery(id+"F0.wireOp",EDGE,"E3.0.13.6"),sQuery(id+"F0.wireOp",EDGE,"E3.0.13.7"),sQuery(id+"F0.wireOp",EDGE,"E3.0.13.8"),sQuery(id+"F0.wireOp",EDGE,"E3.0.13.9"),sQuery(id+"F0.wireOp",EDGE,"E3.0.13.10"),sQuery(id+"F0.wireOp",EDGE,"E3.0.13.11"),sQuery(id+"F0.wireOp",EDGE,"E3.0.13.12"),sQuery(id+"F0.wireOp",EDGE,"E3.0.13.13"),sQuery(id+"F0.wireOp",EDGE,"E3.0.13.14"),sQuery(id+"F0.wireOp",EDGE,"E3.0.13.15"),subQ34,sQuery(id+"F0.wireOp",EDGE,"E3.0.14.0"),sQuery(id+"F0.wireOp",EDGE,"E3.0.14.1"),sQuery(id+"F0.wireOp",EDGE,"E3.0.14.2"),sQuery(id+"F0.wireOp",EDGE,"E3.0.14.3"),sQuery(id+"F0.wireOp",EDGE,"E3.0.14.4"),sQuery(id+"F0.wireOp",EDGE,"E3.0.14.5"),sQuery(id+"F0.wireOp",EDGE,"E3.0.14.6"),sQuery(id+"F0.wireOp",EDGE,"E3.0.14.7"),sQuery(id+"F0.wireOp",EDGE,"E3.0.14.8"),sQuery(id+"F0.wireOp",EDGE,"E3.0.14.9"),sQuery(id+"F0.wireOp",EDGE,"E3.0.14.10"),sQuery(id+"F0.wireOp",EDGE,"E3.0.14.11"),sQuery(id+"F0.wireOp",EDGE,"E3.0.14.12"),sQuery(id+"F0.wireOp",EDGE,"E3.0.14.13"),sQuery(id+"F0.wireOp",EDGE,"E3.0.14.14"),sQuery(id+"F0.wireOp",EDGE,"E3.0.14.15"),subQ11,sQuery(id+"F0.wireOp",EDGE,"E3.0.15.0"),sQuery(id+"F0.wireOp",EDGE,"E3.0.15.1"),sQuery(id+"F0.wireOp",EDGE,"E3.0.15.2"),sQuery(id+"F0.wireOp",EDGE,"E3.0.15.3"),sQuery(id+"F0.wireOp",EDGE,"E3.0.15.4"),sQuery(id+"F0.wireOp",EDGE,"E3.0.15.5"),sQuery(id+"F0.wireOp",EDGE,"E3.0.15.6"),sQuery(id+"F0.wireOp",EDGE,"E3.0.15.7"),sQuery(id+"F0.wireOp",EDGE,"E3.0.15.8"),sQuery(id+"F0.wireOp",EDGE,"E3.0.15.9"),sQuery(id+"F0.wireOp",EDGE,"E3.0.15.10"),sQuery(id+"F0.wireOp",EDGE,"E3.0.15.11"),sQuery(id+"F0.wireOp",EDGE,"E3.0.15.12"),sQuery(id+"F0.wireOp",EDGE,"E3.0.15.13"),sQuery(id+"F0.wireOp",EDGE,"E3.0.15.14"),sQuery(id+"F0.wireOp",EDGE,"E3.0.15.15"),subQ35,sQuery(id+"F0.wireOp",EDGE,"E3.0.16.0"),sQuery(id+"F0.wireOp",EDGE,"E3.0.16.1"),sQuery(id+"F0.wireOp",EDGE,"E3.0.16.2"),sQuery(id+"F0.wireOp",EDGE,"E3.0.16.3"),sQuery(id+"F0.wireOp",EDGE,"E3.0.16.4"),sQuery(id+"F0.wireOp",EDGE,"E3.0.16.5"),sQuery(id+"F0.wireOp",EDGE,"E3.0.16.6"),sQuery(id+"F0.wireOp",EDGE,"E3.0.16.7"),sQuery(id+"F0.wireOp",EDGE,"E3.0.16.8"),sQuery(id+"F0.wireOp",EDGE,"E3.0.16.9"),sQuery(id+"F0.wireOp",EDGE,"E3.0.16.10"),sQuery(id+"F0.wireOp",EDGE,"E3.0.16.11"),sQuery(id+"F0.wireOp",EDGE,"E3.0.16.12"),sQuery(id+"F0.wireOp",EDGE,"E3.0.16.13"),sQuery(id+"F0.wireOp",EDGE,"E3.0.16.14"),sQuery(id+"F0.wireOp",EDGE,"E3.0.16.15"),subQ36])],"isStart":false})});}
            var sketch = newSketch(context, id + "F5", { "sketchPlane" : qUnion([Q0])});
            skPoint(sketch, "E14.orphan", {"position": v(0, 95) * mm});
            skPoint(sketch, "E15.startSnap0", {"position": v(91.88, -83.75) * mm});
            skPoint(sketch, "E16.orphan", {"position": v(95, 0) * mm});
            skLineSegment(sketch, "E17.bottom", {"start": v(-94.7, -94.38) * mm, "end": v(23.3, -94.38) * mm});
            skLineSegment(sketch, "E17.top", {"start": v(-94.7, 20.62) * mm, "end": v(23.3, 20.62) * mm});
            skLineSegment(sketch, "E17.left", {"start": v(-94.7, -94.38) * mm, "end": v(-94.7, 20.62) * mm});
            skLineSegment(sketch, "E17.right", {"start": v(23.3, -94.38) * mm, "end": v(23.3, 20.62) * mm});
            skSolve(sketch);
        }
        {
            var Q0;
            Q0 = qSketchRegion(id + "F5", true);
            extrude(context, id + "F6", {"entities" : qUnion([Q0]), "operationType" : NewBodyOperationType.INTERSECT, "oppositeDirection" : true, "depth" : 25 * mm});
        }
        {
            var Q0;
            {var subQ0=sQuery(id+"F0.wireOp",EDGE,"E3.0.13.0");var subQ1=sQuery(id+"F0.wireOp",EDGE,"E3.0.12.14");var subQ2=sQuery(id+"F0.wireOp",EDGE,"E3.0.12.13");var subQ3=sQuery(id+"F0.wireOp",EDGE,"E3.0.12.12");var subQ4=sQuery(id+"F0.wireOp",EDGE,"E3.0.12.11");var subQ5=sQuery(id+"F0.wireOp",EDGE,"E3.0.12.10");var subQ6=sQuery(id+"F0.wireOp",EDGE,"E3.0.12.9");var subQ7=sQuery(id+"F0.wireOp",EDGE,"E3.0.12.8");var subQ8=sQuery(id+"F0.wireOp",EDGE,"E3.0.12.7");var subQ9=sQuery(id+"F0.wireOp",EDGE,"E3.0.12.6");var subQ10=sQuery(id+"F0.wireOp",EDGE,"E3.0.12.5");var subQ11=sQuery(id+"F0.wireOp",EDGE,"E3.0.12.4");var subQ12=sQuery(id+"F0.wireOp",EDGE,"E3.0.12.3");var subQ13=sQuery(id+"F0.wireOp",EDGE,"E3.0.12.2");var subQ14=sQuery(id+"F0.wireOp",EDGE,"E3.0.12.1");var subQ15=sQuery(id+"F0.wireOp",EDGE,"E3.0.12.0");var subQ16=sQuery(id+"F0.wireOp",EDGE,"E3.0.11.14");var subQ17=sQuery(id+"F0.wireOp",EDGE,"E3.0.11.13");var subQ18=sQuery(id+"F0.wireOp",EDGE,"E3.0.11.12");var subQ19=sQuery(id+"F0.wireOp",EDGE,"E3.0.11.11");var subQ20=sQuery(id+"F0.wireOp",EDGE,"E3.0.11.10");var subQ21=sQuery(id+"F0.wireOp",EDGE,"E3.0.11.9");var subQ22=sQuery(id+"F0.wireOp",EDGE,"E3.0.11.8");var subQ23=sQuery(id+"F0.wireOp",EDGE,"E3.0.11.7");var subQ24=sQuery(id+"F0.wireOp",EDGE,"E3.0.11.6");var subQ25=sQuery(id+"F0.wireOp",EDGE,"E3.0.11.5");var subQ26=sQuery(id+"F0.wireOp",EDGE,"E3.0.11.4");var subQ27=sQuery(id+"F0.wireOp",EDGE,"E3.0.11.3");var subQ28=sQuery(id+"F0.wireOp",EDGE,"E3.0.11.2");var subQ29=sQuery(id+"F0.wireOp",EDGE,"E3.0.11.1");var subQ30=sQuery(id+"F0.wireOp",EDGE,"E3.0.11.0");var subQ31=sQuery(id+"F0.wireOp",EDGE,"E3.0.10.14");var subQ32=sQuery(id+"F0.wireOp",EDGE,"E3.0.10.13");var subQ33=sQuery(id+"F0.wireOp",EDGE,"E3.0.10.12");var subQ34=sQuery(id+"F0.wireOp",EDGE,"E3.0.10.11");var subQ35=sQuery(id+"F0.wireOp",EDGE,"E3.0.10.10");var subQ36=sQuery(id+"F0.wireOp",EDGE,"E3.0.10.9");var subQ37=sQuery(id+"F0.wireOp",EDGE,"E3.0.10.8");var subQ38=sQuery(id+"F0.wireOp",EDGE,"E3.0.10.7");var subQ39=sQuery(id+"F0.wireOp",EDGE,"E3.0.10.6");var subQ40=sQuery(id+"F0.wireOp",EDGE,"E3.0.10.5");var subQ41=sQuery(id+"F0.wireOp",EDGE,"E3.0.10.4");var subQ42=sQuery(id+"F0.wireOp",EDGE,"E3.0.10.3");var subQ43=sQuery(id+"F0.wireOp",EDGE,"E3.0.10.2");var subQ44=sQuery(id+"F0.wireOp",EDGE,"E3.0.10.1");var subQ45=sQuery(id+"F0.wireOp",EDGE,"E3.0.10.0");var subQ46=sQuery(id+"F0.wireOp",EDGE,"E3.0.9.14");var subQ47=sQuery(id+"F0.wireOp",EDGE,"E3.0.9.13");var subQ48=sQuery(id+"F0.wireOp",EDGE,"E3.0.9.12");var subQ49=sQuery(id+"F0.wireOp",EDGE,"E3.0.9.11");var subQ50=sQuery(id+"F0.wireOp",EDGE,"E3.0.9.10");var subQ51=sQuery(id+"F0.wireOp",EDGE,"E3.0.9.9");var subQ52=sQuery(id+"F0.wireOp",EDGE,"E3.0.9.8");var subQ53=sQuery(id+"F0.wireOp",EDGE,"E3.0.9.7");var subQ54=sQuery(id+"F0.wireOp",EDGE,"E3.0.9.6");var subQ55=sQuery(id+"F0.wireOp",EDGE,"E3.0.9.5");var subQ56=sQuery(id+"F0.wireOp",EDGE,"E3.0.9.4");var subQ57=sQuery(id+"F0.wireOp",EDGE,"E3.0.9.3");var subQ58=sQuery(id+"F0.wireOp",EDGE,"E3.0.9.2");var subQ59=sQuery(id+"F0.wireOp",EDGE,"E3.0.9.1");var subQ60=sQuery(id+"F0.wireOp",EDGE,"E3.0.9.0");var subQ61=sQuery(id+"F0.wireOp",EDGE,"E3.0.8.14");var subQ62=sQuery(id+"F0.wireOp",EDGE,"E3.0.8.13");var subQ63=sQuery(id+"F0.wireOp",EDGE,"E3.0.8.12");var subQ64=sQuery(id+"F0.wireOp",EDGE,"E3.0.8.11");var subQ65=sQuery(id+"F0.wireOp",EDGE,"E3.0.8.10");var subQ66=sQuery(id+"F0.wireOp",EDGE,"E3.0.8.9");var subQ67=sQuery(id+"F0.wireOp",EDGE,"E3.0.8.8");var subQ68=sQuery(id+"F0.wireOp",EDGE,"E3.0.8.7");var subQ69=sQuery(id+"F0.wireOp",EDGE,"E3.0.8.6");var subQ70=sQuery(id+"F0.wireOp",EDGE,"E3.0.8.5");var subQ71=sQuery(id+"F0.wireOp",EDGE,"E3.0.8.4");var subQ72=sQuery(id+"F0.wireOp",EDGE,"E3.0.8.3");var subQ73=sQuery(id+"F0.wireOp",EDGE,"E3.0.8.2");var subQ74=sQuery(id+"F0.wireOp",EDGE,"E3.0.8.1");var subQ75=sQuery(id+"F0.wireOp",EDGE,"E3.0.8.0");var subQ76=sQuery(id+"F0.wireOp",EDGE,"E3.0.7.14");var subQ77=sQuery(id+"F0.wireOp",EDGE,"E3.0.7.13");var subQ78=sQuery(id+"F0.wireOp",EDGE,"E3.0.7.12");var subQ79=sQuery(id+"F0.wireOp",EDGE,"E3.0.7.11");var subQ80=sQuery(id+"F0.wireOp",EDGE,"E3.0.7.10");var subQ81=sQuery(id+"F0.wireOp",EDGE,"E3.0.7.9");var subQ82=sQuery(id+"F0.wireOp",EDGE,"E3.0.7.8");var subQ83=sQuery(id+"F0.wireOp",EDGE,"E3.0.7.7");var subQ84=sQuery(id+"F0.wireOp",EDGE,"E3.0.7.6");var subQ85=sQuery(id+"F0.wireOp",EDGE,"E3.0.7.5");var subQ86=sQuery(id+"F0.wireOp",EDGE,"E3.0.7.4");var subQ87=sQuery(id+"F0.wireOp",EDGE,"E3.0.7.3");var subQ88=sQuery(id+"F0.wireOp",EDGE,"E3.0.7.2");var subQ89=sQuery(id+"F0.wireOp",EDGE,"E3.0.7.1");var subQ90=sQuery(id+"F0.wireOp",EDGE,"E3.0.7.0");var subQ91=sQuery(id+"F0.wireOp",EDGE,"E3.0.6.14");var subQ92=sQuery(id+"F0.wireOp",EDGE,"E3.0.6.13");var subQ93=sQuery(id+"F0.wireOp",EDGE,"E3.0.6.12");var subQ94=sQuery(id+"F0.wireOp",EDGE,"E3.0.6.11");var subQ95=sQuery(id+"F0.wireOp",EDGE,"E3.0.6.10");var subQ96=sQuery(id+"F0.wireOp",EDGE,"E3.0.6.9");var subQ97=sQuery(id+"F0.wireOp",EDGE,"E3.0.6.8");var subQ98=sQuery(id+"F0.wireOp",EDGE,"E3.0.6.7");var subQ99=sQuery(id+"F0.wireOp",EDGE,"E3.0.6.6");var subQ100=sQuery(id+"F0.wireOp",EDGE,"E3.0.6.5");var subQ101=sQuery(id+"F0.wireOp",EDGE,"E3.0.2.13");var subQ102=sQuery(id+"F0.wireOp",EDGE,"E3.0.2.12");var subQ103=sQuery(id+"F0.wireOp",EDGE,"E3.0.2.11");var subQ104=sQuery(id+"F0.wireOp",EDGE,"E3.0.2.10");var subQ105=sQuery(id+"F0.wireOp",EDGE,"E3.0.2.9");var subQ106=sQuery(id+"F0.wireOp",EDGE,"E3.0.2.8");var subQ107=sQuery(id+"F0.wireOp",EDGE,"E3.0.2.7");var subQ108=sQuery(id+"F0.wireOp",EDGE,"E3.0.2.6");var subQ109=sQuery(id+"F0.wireOp",EDGE,"E3.0.2.5");var subQ110=sQuery(id+"F0.wireOp",EDGE,"E3.0.2.4");var subQ111=sQuery(id+"F0.wireOp",EDGE,"E3.0.2.3");var subQ112=sQuery(id+"F0.wireOp",EDGE,"E3.0.2.2");var subQ113=sQuery(id+"F0.wireOp",EDGE,"E3.0.2.1");var subQ114=sQuery(id+"F0.wireOp",EDGE,"E3.0.2.0");var subQ115=sQuery(id+"F0.wireOp",EDGE,"E3.0.1.14");var subQ116=sQuery(id+"F0.wireOp",EDGE,"E3.0.1.13");var subQ117=sQuery(id+"F0.wireOp",EDGE,"E3.0.1.12");var subQ118=sQuery(id+"F0.wireOp",EDGE,"E3.0.1.11");var subQ119=sQuery(id+"F0.wireOp",EDGE,"E3.0.1.10");var subQ120=sQuery(id+"F0.wireOp",EDGE,"E3.0.1.9");var subQ121=sQuery(id+"F0.wireOp",EDGE,"E3.0.1.8");var subQ122=sQuery(id+"F0.wireOp",EDGE,"E3.0.1.7");var subQ123=sQuery(id+"F0.wireOp",EDGE,"E3.0.1.6");var subQ124=sQuery(id+"F0.wireOp",EDGE,"E2.0.7.0");var subQ125=sQuery(id+"F0.wireOp",EDGE,"E2.0.6.0");var subQ126=sQuery(id+"F0.wireOp",EDGE,"E2.0.5.0");var subQ127=sQuery(id+"F0.wireOp",EDGE,"E2.0.4.0");var subQ128=sQuery(id+"F0.wireOp",EDGE,"E2.0.3.0");var subQ129=sQuery(id+"F0.wireOp",EDGE,"E2.0.2.0");var subQ130=sQuery(id+"F0.wireOp",EDGE,"E3.0.2.14");var subQ131=sQuery(id+"F0.wireOp",EDGE,"E3.0.13.1");var subQ132=sQuery(id+"F0.wireOp",EDGE,"E0.top");var subQ133=sQuery(id+"F0.wireOp",EDGE,"E3.0.6.4");var subQ134=sQuery(id+"F0.wireOp",EDGE,"E3.0.1.5");var subQ135=sQuery(id+"F0.wireOp",EDGE,"E0.right");var subQ136=sQuery(id+"F0.wireOp",EDGE,"E1");var subQ137=sQuery(id+"F0.wireOp",EDGE,"E2.0.1.0");var subQ138=sQuery(id+"F0.wireOp",EDGE,"E2.0.8.0");var subQ139=sQuery(id+"F0.wireOp",EDGE,"E2.0.9.0");var subQ140=sQuery(id+"F0.wireOp",EDGE,"E2.0.10.0");var subQ141=sQuery(id+"F0.wireOp",EDGE,"E2.0.11.0");var subQ142=sQuery(id+"F0.wireOp",EDGE,"E2.0.12.0");var subQ143=sQuery(id+"F0.wireOp",EDGE,"E2.0.13.0");var subQ144=sQuery(id+"F0.wireOp",EDGE,"E3.0.1.0");var subQ145=sQuery(id+"F0.wireOp",EDGE,"E3.0.1.1");var subQ146=sQuery(id+"F0.wireOp",EDGE,"E3.0.1.2");var subQ147=sQuery(id+"F0.wireOp",EDGE,"E3.0.1.3");var subQ148=sQuery(id+"F0.wireOp",EDGE,"E3.0.1.4");var subQ149=sQuery(id+"F0.wireOp",EDGE,"E3.0.3.0");var subQ150=sQuery(id+"F0.wireOp",EDGE,"E3.0.3.1");var subQ151=sQuery(id+"F0.wireOp",EDGE,"E3.0.3.2");var subQ152=sQuery(id+"F0.wireOp",EDGE,"E3.0.3.3");var subQ153=sQuery(id+"F0.wireOp",EDGE,"E3.0.3.4");var subQ154=sQuery(id+"F0.wireOp",EDGE,"E3.0.3.5");var subQ155=sQuery(id+"F0.wireOp",EDGE,"E3.0.3.6");var subQ156=sQuery(id+"F0.wireOp",EDGE,"E3.0.3.7");var subQ157=sQuery(id+"F0.wireOp",EDGE,"E3.0.3.8");var subQ158=sQuery(id+"F0.wireOp",EDGE,"E3.0.3.9");var subQ159=sQuery(id+"F0.wireOp",EDGE,"E3.0.3.10");var subQ160=sQuery(id+"F0.wireOp",EDGE,"E3.0.3.11");var subQ161=sQuery(id+"F0.wireOp",EDGE,"E3.0.3.12");var subQ162=sQuery(id+"F0.wireOp",EDGE,"E3.0.3.13");var subQ163=sQuery(id+"F0.wireOp",EDGE,"E3.0.3.14");var subQ164=sQuery(id+"F0.wireOp",EDGE,"E3.0.4.0");var subQ165=sQuery(id+"F0.wireOp",EDGE,"E3.0.4.1");var subQ166=sQuery(id+"F0.wireOp",EDGE,"E3.0.4.2");var subQ167=sQuery(id+"F0.wireOp",EDGE,"E3.0.4.3");var subQ168=sQuery(id+"F0.wireOp",EDGE,"E3.0.4.4");var subQ169=sQuery(id+"F0.wireOp",EDGE,"E3.0.4.5");var subQ170=sQuery(id+"F0.wireOp",EDGE,"E3.0.4.6");var subQ171=sQuery(id+"F0.wireOp",EDGE,"E3.0.4.7");var subQ172=sQuery(id+"F0.wireOp",EDGE,"E3.0.4.8");var subQ173=sQuery(id+"F0.wireOp",EDGE,"E3.0.4.9");var subQ174=sQuery(id+"F0.wireOp",EDGE,"E3.0.4.10");var subQ175=sQuery(id+"F0.wireOp",EDGE,"E3.0.4.11");var subQ176=sQuery(id+"F0.wireOp",EDGE,"E3.0.4.12");var subQ177=sQuery(id+"F0.wireOp",EDGE,"E3.0.4.13");var subQ178=sQuery(id+"F0.wireOp",EDGE,"E3.0.4.14");var subQ179=sQuery(id+"F0.wireOp",EDGE,"E3.0.5.0");var subQ180=sQuery(id+"F0.wireOp",EDGE,"E3.0.5.1");var subQ181=sQuery(id+"F0.wireOp",EDGE,"E3.0.5.2");var subQ182=sQuery(id+"F0.wireOp",EDGE,"E3.0.5.3");var subQ183=sQuery(id+"F0.wireOp",EDGE,"E3.0.5.4");var subQ184=sQuery(id+"F0.wireOp",EDGE,"E3.0.5.5");var subQ185=sQuery(id+"F0.wireOp",EDGE,"E3.0.5.6");var subQ186=sQuery(id+"F0.wireOp",EDGE,"E3.0.5.7");var subQ187=sQuery(id+"F0.wireOp",EDGE,"E3.0.5.8");var subQ188=sQuery(id+"F0.wireOp",EDGE,"E3.0.5.9");var subQ189=sQuery(id+"F0.wireOp",EDGE,"E3.0.5.10");var subQ190=sQuery(id+"F0.wireOp",EDGE,"E3.0.5.11");var subQ191=sQuery(id+"F0.wireOp",EDGE,"E3.0.5.12");var subQ192=sQuery(id+"F0.wireOp",EDGE,"E3.0.5.13");var subQ193=sQuery(id+"F0.wireOp",EDGE,"E3.0.5.14");var subQ194=sQuery(id+"F0.wireOp",EDGE,"E3.0.6.0");var subQ195=sQuery(id+"F0.wireOp",EDGE,"E3.0.6.1");var subQ196=sQuery(id+"F0.wireOp",EDGE,"E3.0.6.2");var subQ197=sQuery(id+"F0.wireOp",EDGE,"E3.0.6.3");var subQ198=sQuery(id+"F0.wireOp",EDGE,"E3.0.13.2");var subQ199=sQuery(id+"F0.wireOp",EDGE,"E3.0.13.3");var subQ200=sQuery(id+"F0.wireOp",EDGE,"E3.0.13.4");var subQ201=sQuery(id+"F0.wireOp",EDGE,"E3.0.13.5");var subQ202=sQuery(id+"F0.wireOp",EDGE,"E3.0.13.6");var subQ203=sQuery(id+"F0.wireOp",EDGE,"E3.0.13.7");var subQ204=sQuery(id+"F0.wireOp",EDGE,"E3.0.13.8");var subQ205=sQuery(id+"F0.wireOp",EDGE,"E3.0.13.9");var subQ206=sQuery(id+"F0.wireOp",EDGE,"E3.0.13.10");var subQ207=sQuery(id+"F0.wireOp",EDGE,"E3.0.13.11");var subQ208=sQuery(id+"F0.wireOp",EDGE,"E3.0.13.12");var subQ209=sQuery(id+"F0.wireOp",EDGE,"E3.0.13.13");var subQ210=sQuery(id+"F0.wireOp",EDGE,"E3.0.13.14");var subQ211=sQuery(id+"F0.wireOp",EDGE,"E3.0.14.0");var subQ212=sQuery(id+"F0.wireOp",EDGE,"E3.0.14.1");var subQ213=sQuery(id+"F0.wireOp",EDGE,"E3.0.14.2");var subQ214=sQuery(id+"F0.wireOp",EDGE,"E3.0.14.3");var subQ215=sQuery(id+"F0.wireOp",EDGE,"E3.0.14.4");var subQ216=sQuery(id+"F0.wireOp",EDGE,"E3.0.14.5");var subQ217=sQuery(id+"F0.wireOp",EDGE,"E3.0.14.6");var subQ218=sQuery(id+"F0.wireOp",EDGE,"E3.0.14.7");var subQ219=sQuery(id+"F0.wireOp",EDGE,"E3.0.14.8");var subQ220=sQuery(id+"F0.wireOp",EDGE,"E3.0.14.9");var subQ221=sQuery(id+"F0.wireOp",EDGE,"E3.0.14.10");var subQ222=sQuery(id+"F0.wireOp",EDGE,"E3.0.14.11");var subQ223=sQuery(id+"F0.wireOp",EDGE,"E3.0.14.12");var subQ224=sQuery(id+"F0.wireOp",EDGE,"E3.0.14.13");var subQ225=sQuery(id+"F0.wireOp",EDGE,"E3.0.14.14");Q0=makeQuery(id+"FJqtpdUANZnq3Um_1.boolean.opBoolean","SPLIT",FACE,{"disambiguationData":[TD([makeQuery(id+"F1.opExtrude","SWEPT_FACE",FACE,{"disambiguationData":[OSD([subQ144])]})])],"derivedFrom":makeQuery(id+"F1.opExtrude","CAP_FACE",FACE,{"disambiguationData":[OSD([sQuery(id+"F0.wireOp",EDGE,"E0.bottom"),subQ132,sQuery(id+"F0.wireOp",EDGE,"E0.left"),subQ135,subQ136,subQ137,subQ129,subQ128,subQ127,subQ126,subQ125,subQ124,subQ138,subQ139,subQ140,subQ141,subQ142,subQ143,sQuery(id+"F0.wireOp",EDGE,"E2.0.14.0"),subQ144,subQ145,subQ146,subQ147,subQ148,subQ134,subQ123,subQ122,subQ121,subQ120,subQ119,subQ118,subQ117,subQ116,subQ115,subQ114,subQ113,subQ112,subQ111,subQ110,subQ109,subQ108,subQ107,subQ106,subQ105,subQ104,subQ103,subQ102,subQ101,subQ130,subQ149,subQ150,subQ151,subQ152,subQ153,subQ154,subQ155,subQ156,subQ157,subQ158,subQ159,subQ160,subQ161,subQ162,subQ163,subQ164,subQ165,subQ166,subQ167,subQ168,subQ169,subQ170,subQ171,subQ172,subQ173,subQ174,subQ175,subQ176,subQ177,subQ178,subQ179,subQ180,subQ181,subQ182,subQ183,subQ184,subQ185,subQ186,subQ187,subQ188,subQ189,subQ190,subQ191,subQ192,subQ193,subQ194,subQ195,subQ196,subQ197,subQ133,subQ100,subQ99,subQ98,subQ97,subQ96,subQ95,subQ94,subQ93,subQ92,subQ91,subQ90,subQ89,subQ88,subQ87,subQ86,subQ85,subQ84,subQ83,subQ82,subQ81,subQ80,subQ79,subQ78,subQ77,subQ76,subQ75,subQ74,subQ73,subQ72,subQ71,subQ70,subQ69,subQ68,subQ67,subQ66,subQ65,subQ64,subQ63,subQ62,subQ61,subQ60,subQ59,subQ58,subQ57,subQ56,subQ55,subQ54,subQ53,subQ52,subQ51,subQ50,subQ49,subQ48,subQ47,subQ46,subQ45,subQ44,subQ43,subQ42,subQ41,subQ40,subQ39,subQ38,subQ37,subQ36,subQ35,subQ34,subQ33,subQ32,subQ31,subQ30,subQ29,subQ28,subQ27,subQ26,subQ25,subQ24,subQ23,subQ22,subQ21,subQ20,subQ19,subQ18,subQ17,subQ16,subQ15,subQ14,subQ13,subQ12,subQ11,subQ10,subQ9,subQ8,subQ7,subQ6,subQ5,subQ4,subQ3,subQ2,subQ1,subQ0,subQ131,subQ198,subQ199,subQ200,subQ201,subQ202,subQ203,subQ204,subQ205,subQ206,subQ207,subQ208,subQ209,subQ210,subQ211,subQ212,subQ213,subQ214,subQ215,subQ216,subQ217,subQ218,subQ219,subQ220,subQ221,subQ222,subQ223,subQ224,subQ225])],"isStart":false})});}
            var sketch = newSketch(context, id + "F7", { "sketchPlane" : qUnion([Q0])});
            skCircle(sketch, "E18", {"center": v(-80, 37) * mm, "radius": 2 * mm});
            skCircle(sketch, "E19.0.1.0", {"center": v(-80, 25) * mm, "radius": 2 * mm});
            skCircle(sketch, "E19.0.2.0", {"center": v(-80, 13) * mm, "radius": 2 * mm});
            skCircle(sketch, "E19.0.3.0", {"center": v(-80, 1) * mm, "radius": 2 * mm});
            skCircle(sketch, "E19.0.4.0", {"center": v(-80, -11) * mm, "radius": 2 * mm});
            skCircle(sketch, "E19.0.5.0", {"center": v(-80, -23) * mm, "radius": 2 * mm});
            skCircle(sketch, "E19.0.6.0", {"center": v(-80, -35) * mm, "radius": 2 * mm});
            skCircle(sketch, "E19.0.7.0", {"center": v(-80, -47) * mm, "radius": 2 * mm});
            skCircle(sketch, "E19.0.8.0", {"center": v(-80, -59) * mm, "radius": 2 * mm});
            skCircle(sketch, "E19.0.9.0", {"center": v(-80, -71) * mm, "radius": 2 * mm});
            skCircle(sketch, "E19.0.10.0", {"center": v(-80, -83) * mm, "radius": 2 * mm});
            skCircle(sketch, "E19.1.0.0", {"center": v(-68, 37) * mm, "radius": 2 * mm});
            skCircle(sketch, "E19.1.1.0", {"center": v(-68, 25) * mm, "radius": 2 * mm});
            skCircle(sketch, "E19.1.2.0", {"center": v(-68, 13) * mm, "radius": 2 * mm});
            skCircle(sketch, "E19.1.3.0", {"center": v(-68, 1) * mm, "radius": 2 * mm});
            skCircle(sketch, "E19.1.4.0", {"center": v(-68, -11) * mm, "radius": 2 * mm});
            skCircle(sketch, "E19.1.5.0", {"center": v(-68, -23) * mm, "radius": 2 * mm});
            skCircle(sketch, "E19.1.6.0", {"center": v(-68, -35) * mm, "radius": 2 * mm});
            skCircle(sketch, "E19.1.7.0", {"center": v(-68, -47) * mm, "radius": 2 * mm});
            skCircle(sketch, "E19.1.8.0", {"center": v(-68, -59) * mm, "radius": 2 * mm});
            skCircle(sketch, "E19.1.9.0", {"center": v(-68, -71) * mm, "radius": 2 * mm});
            skCircle(sketch, "E19.1.10.0", {"center": v(-68, -83) * mm, "radius": 2 * mm});
            skCircle(sketch, "E19.2.0.0", {"center": v(-56, 37) * mm, "radius": 2 * mm});
            skCircle(sketch, "E19.2.1.0", {"center": v(-56, 25) * mm, "radius": 2 * mm});
            skCircle(sketch, "E19.2.2.0", {"center": v(-56, 13) * mm, "radius": 2 * mm});
            skCircle(sketch, "E19.2.3.0", {"center": v(-56, 1) * mm, "radius": 2 * mm});
            skCircle(sketch, "E19.2.4.0", {"center": v(-56, -11) * mm, "radius": 2 * mm});
            skCircle(sketch, "E19.2.5.0", {"center": v(-56, -23) * mm, "radius": 2 * mm});
            skCircle(sketch, "E19.2.6.0", {"center": v(-56, -35) * mm, "radius": 2 * mm});
            skCircle(sketch, "E19.2.7.0", {"center": v(-56, -47) * mm, "radius": 2 * mm});
            skCircle(sketch, "E19.2.8.0", {"center": v(-56, -59) * mm, "radius": 2 * mm});
            skCircle(sketch, "E19.2.9.0", {"center": v(-56, -71) * mm, "radius": 2 * mm});
            skCircle(sketch, "E19.2.10.0", {"center": v(-56, -83) * mm, "radius": 2 * mm});
            skCircle(sketch, "E19.3.0.0", {"center": v(-44, 37) * mm, "radius": 2 * mm});
            skCircle(sketch, "E19.3.1.0", {"center": v(-44, 25) * mm, "radius": 2 * mm});
            skCircle(sketch, "E19.3.2.0", {"center": v(-44, 13) * mm, "radius": 2 * mm});
            skCircle(sketch, "E19.3.3.0", {"center": v(-44, 1) * mm, "radius": 2 * mm});
            skCircle(sketch, "E19.3.4.0", {"center": v(-44, -11) * mm, "radius": 2 * mm});
            skCircle(sketch, "E19.3.5.0", {"center": v(-44, -23) * mm, "radius": 2 * mm});
            skCircle(sketch, "E19.3.6.0", {"center": v(-44, -35) * mm, "radius": 2 * mm});
            skCircle(sketch, "E19.3.7.0", {"center": v(-44, -47) * mm, "radius": 2 * mm});
            skCircle(sketch, "E19.3.8.0", {"center": v(-44, -59) * mm, "radius": 2 * mm});
            skCircle(sketch, "E19.3.9.0", {"center": v(-44, -71) * mm, "radius": 2 * mm});
            skCircle(sketch, "E19.3.10.0", {"center": v(-44, -83) * mm, "radius": 2 * mm});
            skCircle(sketch, "E19.4.0.0", {"center": v(-32, 37) * mm, "radius": 2 * mm});
            skCircle(sketch, "E19.4.1.0", {"center": v(-32, 25) * mm, "radius": 2 * mm});
            skCircle(sketch, "E19.4.2.0", {"center": v(-32, 13) * mm, "radius": 2 * mm});
            skCircle(sketch, "E19.4.3.0", {"center": v(-32, 1) * mm, "radius": 2 * mm});
            skCircle(sketch, "E19.4.4.0", {"center": v(-32, -11) * mm, "radius": 2 * mm});
            skCircle(sketch, "E19.4.5.0", {"center": v(-32, -23) * mm, "radius": 2 * mm});
            skCircle(sketch, "E19.4.6.0", {"center": v(-32, -35) * mm, "radius": 2 * mm});
            skCircle(sketch, "E19.4.7.0", {"center": v(-32, -47) * mm, "radius": 2 * mm});
            skCircle(sketch, "E19.4.8.0", {"center": v(-32, -59) * mm, "radius": 2 * mm});
            skCircle(sketch, "E19.4.9.0", {"center": v(-32, -71) * mm, "radius": 2 * mm});
            skCircle(sketch, "E19.4.10.0", {"center": v(-32, -83) * mm, "radius": 2 * mm});
            skCircle(sketch, "E19.5.0.0", {"center": v(-20, 37) * mm, "radius": 2 * mm});
            skCircle(sketch, "E19.5.1.0", {"center": v(-20, 25) * mm, "radius": 2 * mm});
            skCircle(sketch, "E19.5.2.0", {"center": v(-20, 13) * mm, "radius": 2 * mm});
            skCircle(sketch, "E19.5.3.0", {"center": v(-20, 1) * mm, "radius": 2 * mm});
            skCircle(sketch, "E19.5.4.0", {"center": v(-20, -11) * mm, "radius": 2 * mm});
            skCircle(sketch, "E19.5.5.0", {"center": v(-20, -23) * mm, "radius": 2 * mm});
            skCircle(sketch, "E19.5.6.0", {"center": v(-20, -35) * mm, "radius": 2 * mm});
            skCircle(sketch, "E19.5.7.0", {"center": v(-20, -47) * mm, "radius": 2 * mm});
            skCircle(sketch, "E19.5.8.0", {"center": v(-20, -59) * mm, "radius": 2 * mm});
            skCircle(sketch, "E19.5.9.0", {"center": v(-20, -71) * mm, "radius": 2 * mm});
            skCircle(sketch, "E19.5.10.0", {"center": v(-20, -83) * mm, "radius": 2 * mm});
            skCircle(sketch, "E19.6.0.0", {"center": v(-8, 37) * mm, "radius": 2 * mm});
            skCircle(sketch, "E19.6.1.0", {"center": v(-8, 25) * mm, "radius": 2 * mm});
            skCircle(sketch, "E19.6.2.0", {"center": v(-8, 13) * mm, "radius": 2 * mm});
            skCircle(sketch, "E19.6.3.0", {"center": v(-8, 1) * mm, "radius": 2 * mm});
            skCircle(sketch, "E19.6.4.0", {"center": v(-8, -11) * mm, "radius": 2 * mm});
            skCircle(sketch, "E19.6.5.0", {"center": v(-8, -23) * mm, "radius": 2 * mm});
            skCircle(sketch, "E19.6.6.0", {"center": v(-8, -35) * mm, "radius": 2 * mm});
            skCircle(sketch, "E19.6.7.0", {"center": v(-8, -47) * mm, "radius": 2 * mm});
            skCircle(sketch, "E19.6.8.0", {"center": v(-8, -59) * mm, "radius": 2 * mm});
            skCircle(sketch, "E19.6.9.0", {"center": v(-8, -71) * mm, "radius": 2 * mm});
            skCircle(sketch, "E19.6.10.0", {"center": v(-8, -83) * mm, "radius": 2 * mm});
            skCircle(sketch, "E19.7.0.0", {"center": v(4, 37) * mm, "radius": 2 * mm});
            skCircle(sketch, "E19.7.1.0", {"center": v(4, 25) * mm, "radius": 2 * mm});
            skCircle(sketch, "E19.7.2.0", {"center": v(4, 13) * mm, "radius": 2 * mm});
            skCircle(sketch, "E19.7.3.0", {"center": v(4, 1) * mm, "radius": 2 * mm});
            skCircle(sketch, "E19.7.4.0", {"center": v(4, -11) * mm, "radius": 2 * mm});
            skCircle(sketch, "E19.7.5.0", {"center": v(4, -23) * mm, "radius": 2 * mm});
            skCircle(sketch, "E19.7.6.0", {"center": v(4, -35) * mm, "radius": 2 * mm});
            skCircle(sketch, "E19.7.7.0", {"center": v(4, -47) * mm, "radius": 2 * mm});
            skCircle(sketch, "E19.7.8.0", {"center": v(4, -59) * mm, "radius": 2 * mm});
            skCircle(sketch, "E19.7.9.0", {"center": v(4, -71) * mm, "radius": 2 * mm});
            skCircle(sketch, "E19.7.10.0", {"center": v(4, -83) * mm, "radius": 2 * mm});
            skCircle(sketch, "E19.8.0.0", {"center": v(16, 37) * mm, "radius": 2 * mm});
            skCircle(sketch, "E19.8.1.0", {"center": v(16, 25) * mm, "radius": 2 * mm});
            skCircle(sketch, "E19.8.2.0", {"center": v(16, 13) * mm, "radius": 2 * mm});
            skCircle(sketch, "E19.8.3.0", {"center": v(16, 1) * mm, "radius": 2 * mm});
            skCircle(sketch, "E19.8.4.0", {"center": v(16, -11) * mm, "radius": 2 * mm});
            skCircle(sketch, "E19.8.5.0", {"center": v(16, -23) * mm, "radius": 2 * mm});
            skCircle(sketch, "E19.8.6.0", {"center": v(16, -35) * mm, "radius": 2 * mm});
            skCircle(sketch, "E19.8.7.0", {"center": v(16, -47) * mm, "radius": 2 * mm});
            skCircle(sketch, "E19.8.8.0", {"center": v(16, -59) * mm, "radius": 2 * mm});
            skCircle(sketch, "E19.8.9.0", {"center": v(16, -71) * mm, "radius": 2 * mm});
            skCircle(sketch, "E19.8.10.0", {"center": v(16, -83) * mm, "radius": 2 * mm});
            skCircle(sketch, "E19.9.0.0", {"center": v(28, 37) * mm, "radius": 2 * mm});
            skCircle(sketch, "E19.9.1.0", {"center": v(28, 25) * mm, "radius": 2 * mm});
            skCircle(sketch, "E19.9.2.0", {"center": v(28, 13) * mm, "radius": 2 * mm});
            skCircle(sketch, "E19.9.3.0", {"center": v(28, 1) * mm, "radius": 2 * mm});
            skCircle(sketch, "E19.9.4.0", {"center": v(28, -11) * mm, "radius": 2 * mm});
            skCircle(sketch, "E19.9.5.0", {"center": v(28, -23) * mm, "radius": 2 * mm});
            skCircle(sketch, "E19.9.6.0", {"center": v(28, -35) * mm, "radius": 2 * mm});
            skCircle(sketch, "E19.9.7.0", {"center": v(28, -47) * mm, "radius": 2 * mm});
            skCircle(sketch, "E19.9.8.0", {"center": v(28, -59) * mm, "radius": 2 * mm});
            skCircle(sketch, "E19.9.9.0", {"center": v(28, -71) * mm, "radius": 2 * mm});
            skCircle(sketch, "E19.9.10.0", {"center": v(28, -83) * mm, "radius": 2 * mm});
            skCircle(sketch, "E19.10.0.0", {"center": v(40, 37) * mm, "radius": 2 * mm});
            skCircle(sketch, "E19.10.1.0", {"center": v(40, 25) * mm, "radius": 2 * mm});
            skCircle(sketch, "E19.10.2.0", {"center": v(40, 13) * mm, "radius": 2 * mm});
            skCircle(sketch, "E19.10.3.0", {"center": v(40, 1) * mm, "radius": 2 * mm});
            skCircle(sketch, "E19.10.4.0", {"center": v(40, -11) * mm, "radius": 2 * mm});
            skCircle(sketch, "E19.10.5.0", {"center": v(40, -23) * mm, "radius": 2 * mm});
            skCircle(sketch, "E19.10.6.0", {"center": v(40, -35) * mm, "radius": 2 * mm});
            skCircle(sketch, "E19.10.7.0", {"center": v(40, -47) * mm, "radius": 2 * mm});
            skCircle(sketch, "E19.10.8.0", {"center": v(40, -59) * mm, "radius": 2 * mm});
            skCircle(sketch, "E19.10.9.0", {"center": v(40, -71) * mm, "radius": 2 * mm});
            skCircle(sketch, "E19.10.10.0", {"center": v(40, -83) * mm, "radius": 2 * mm});
            skLineSegment(sketch, "E19.direction1", {"start": v(-80, 37) * mm, "end": v(-68, 37) * mm, "construction": true});
            skLineSegment(sketch, "E19.direction2", {"start": v(-80, 37) * mm, "end": v(-80, 25) * mm, "construction": true});
            skSolve(sketch);
        }
        {
            var Q0;
            Q0 = qSketchRegion(id + "F7", true);
            extrude(context, id + "F8", {"entities" : qUnion([Q0]), "operationType" : NewBodyOperationType.REMOVE, "oppositeDirection" : true, "depth" : 1.5 * mm});
        }
        {
            var Q0;
            Q0 = qSketchRegion(id + "F2", true);
            extrude(context, id + "F9", {"entities" : qUnion([Q0]), "operationType" : NewBodyOperationType.REMOVE, "oppositeDirection" : true, "depth" : 1 * mm});
        }
        {
            var Q0;
            Q0 = qSketchRegion(id + "F3", true);
            extrude(context, id + "F10", {"entities" : qUnion([Q0]), "operationType" : NewBodyOperationType.REMOVE, "oppositeDirection" : true, "depth" : 1 * mm});
        }
        {
            var Q0;
            Q0 = qSketchRegion(id + "F4", true);
            extrude(context, id + "F11", {"entities" : qUnion([Q0]), "operationType" : NewBodyOperationType.REMOVE, "oppositeDirection" : true, "depth" : 1 * mm});
        }
    });
